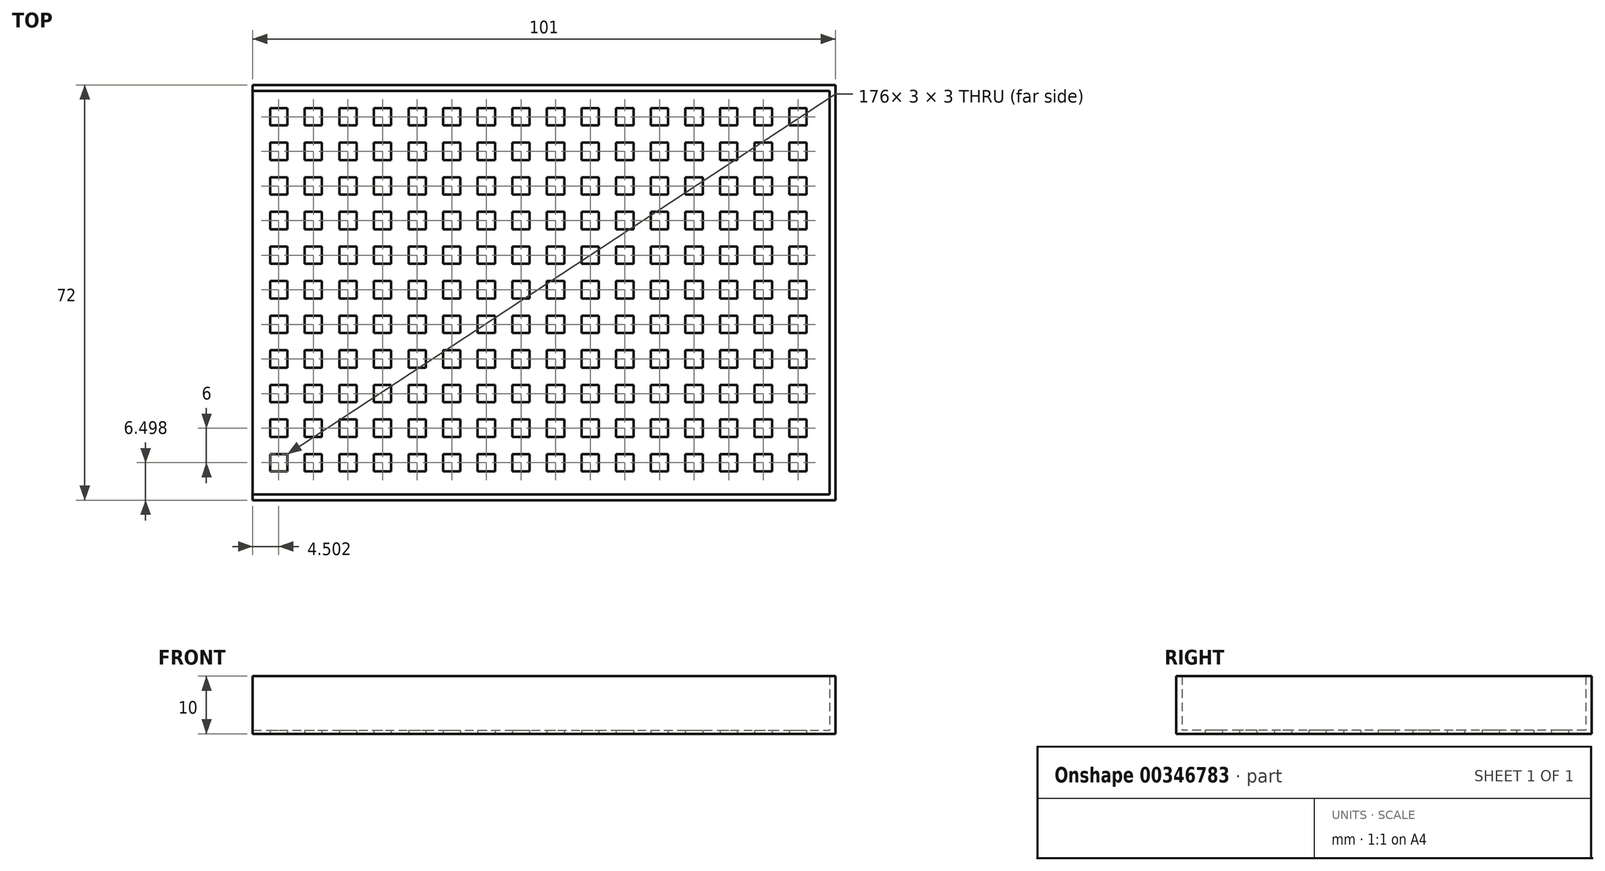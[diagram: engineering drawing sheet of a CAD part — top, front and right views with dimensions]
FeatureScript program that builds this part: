
annotation { "Feature Type Name" : "Feature", "Feature Type Description" : "" }
export const myFeature = defineFeature(function(context is Context, id is Id, definition is map)
    precondition{}
    {
        {
            var Q0;
            Q0=qCreatedBy(makeId("Top.planeOp"),FACE);
            var sketch = newSketch(context, id + "F0", { "sketchPlane" : qUnion([Q0])});
            skLineSegment(sketch, "E0.bottom", {"start": v(-89.09, 32.87) * mm, "end": v(10.91, 32.87) * mm});
            skLineSegment(sketch, "E0.top", {"start": v(-89.09, -37.13) * mm, "end": v(10.91, -37.13) * mm});
            skLineSegment(sketch, "E0.left", {"start": v(-89.09, 32.87) * mm, "end": v(-89.09, -37.13) * mm});
            skLineSegment(sketch, "E0.right", {"start": v(10.91, 32.87) * mm, "end": v(10.91, -37.13) * mm});
            skLineSegment(sketch, "E1.bottom", {"start": v(11.91, -38.13) * mm, "end": v(-89.09, -38.13) * mm});
            skLineSegment(sketch, "E1.top", {"start": v(11.91, 33.87) * mm, "end": v(-89.09, 33.87) * mm});
            skLineSegment(sketch, "E1.left", {"start": v(11.91, -38.13) * mm, "end": v(11.91, 33.87) * mm});
            skLineSegment(sketch, "E1.right", {"start": v(-89.09, -38.13) * mm, "end": v(-89.09, 33.87) * mm});
            skLineSegment(sketch, "E2.bottom", {"start": v(-86.09, 29.87) * mm, "end": v(-83.09, 29.87) * mm});
            skLineSegment(sketch, "E2.top", {"start": v(-86.09, 26.87) * mm, "end": v(-83.09, 26.87) * mm});
            skLineSegment(sketch, "E2.left", {"start": v(-86.09, 29.87) * mm, "end": v(-86.09, 26.87) * mm});
            skLineSegment(sketch, "E2.right", {"start": v(-83.09, 29.87) * mm, "end": v(-83.09, 26.87) * mm});
            skLineSegment(sketch, "E3.0.1.0", {"start": v(-86.09, 23.87) * mm, "end": v(-83.09, 23.87) * mm});
            skLineSegment(sketch, "E3.0.1.1", {"start": v(-86.09, 20.87) * mm, "end": v(-83.09, 20.87) * mm});
            skLineSegment(sketch, "E3.0.1.2", {"start": v(-86.09, 23.87) * mm, "end": v(-86.09, 20.87) * mm});
            skLineSegment(sketch, "E3.0.1.3", {"start": v(-83.09, 23.87) * mm, "end": v(-83.09, 20.87) * mm});
            skLineSegment(sketch, "E3.0.2.0", {"start": v(-86.09, 17.87) * mm, "end": v(-83.09, 17.87) * mm});
            skLineSegment(sketch, "E3.0.2.1", {"start": v(-86.09, 14.87) * mm, "end": v(-83.09, 14.87) * mm});
            skLineSegment(sketch, "E3.0.2.2", {"start": v(-86.09, 17.87) * mm, "end": v(-86.09, 14.87) * mm});
            skLineSegment(sketch, "E3.0.2.3", {"start": v(-83.09, 17.87) * mm, "end": v(-83.09, 14.87) * mm});
            skLineSegment(sketch, "E3.0.3.0", {"start": v(-86.09, 11.87) * mm, "end": v(-83.09, 11.87) * mm});
            skLineSegment(sketch, "E3.0.3.1", {"start": v(-86.09, 8.87) * mm, "end": v(-83.09, 8.87) * mm});
            skLineSegment(sketch, "E3.0.3.2", {"start": v(-86.09, 11.87) * mm, "end": v(-86.09, 8.87) * mm});
            skLineSegment(sketch, "E3.0.3.3", {"start": v(-83.09, 11.87) * mm, "end": v(-83.09, 8.87) * mm});
            skLineSegment(sketch, "E3.0.4.0", {"start": v(-86.09, 5.87) * mm, "end": v(-83.09, 5.87) * mm});
            skLineSegment(sketch, "E3.0.4.1", {"start": v(-86.09, 2.87) * mm, "end": v(-83.09, 2.87) * mm});
            skLineSegment(sketch, "E3.0.4.2", {"start": v(-86.09, 5.87) * mm, "end": v(-86.09, 2.87) * mm});
            skLineSegment(sketch, "E3.0.4.3", {"start": v(-83.09, 5.87) * mm, "end": v(-83.09, 2.87) * mm});
            skLineSegment(sketch, "E3.0.5.0", {"start": v(-86.09, -0.13) * mm, "end": v(-83.09, -0.13) * mm});
            skLineSegment(sketch, "E3.0.5.1", {"start": v(-86.09, -3.13) * mm, "end": v(-83.09, -3.13) * mm});
            skLineSegment(sketch, "E3.0.5.2", {"start": v(-86.09, -0.13) * mm, "end": v(-86.09, -3.13) * mm});
            skLineSegment(sketch, "E3.0.5.3", {"start": v(-83.09, -0.13) * mm, "end": v(-83.09, -3.13) * mm});
            skLineSegment(sketch, "E3.0.6.0", {"start": v(-86.09, -6.13) * mm, "end": v(-83.09, -6.13) * mm});
            skLineSegment(sketch, "E3.0.6.1", {"start": v(-86.09, -9.13) * mm, "end": v(-83.09, -9.13) * mm});
            skLineSegment(sketch, "E3.0.6.2", {"start": v(-86.09, -6.13) * mm, "end": v(-86.09, -9.13) * mm});
            skLineSegment(sketch, "E3.0.6.3", {"start": v(-83.09, -6.13) * mm, "end": v(-83.09, -9.13) * mm});
            skLineSegment(sketch, "E3.0.7.0", {"start": v(-86.09, -12.13) * mm, "end": v(-83.09, -12.13) * mm});
            skLineSegment(sketch, "E3.0.7.1", {"start": v(-86.09, -15.13) * mm, "end": v(-83.09, -15.13) * mm});
            skLineSegment(sketch, "E3.0.7.2", {"start": v(-86.09, -12.13) * mm, "end": v(-86.09, -15.13) * mm});
            skLineSegment(sketch, "E3.0.7.3", {"start": v(-83.09, -12.13) * mm, "end": v(-83.09, -15.13) * mm});
            skLineSegment(sketch, "E3.0.8.0", {"start": v(-86.09, -18.13) * mm, "end": v(-83.09, -18.13) * mm});
            skLineSegment(sketch, "E3.0.8.1", {"start": v(-86.09, -21.13) * mm, "end": v(-83.09, -21.13) * mm});
            skLineSegment(sketch, "E3.0.8.2", {"start": v(-86.09, -18.13) * mm, "end": v(-86.09, -21.13) * mm});
            skLineSegment(sketch, "E3.0.8.3", {"start": v(-83.09, -18.13) * mm, "end": v(-83.09, -21.13) * mm});
            skLineSegment(sketch, "E3.0.9.0", {"start": v(-86.09, -24.13) * mm, "end": v(-83.09, -24.13) * mm});
            skLineSegment(sketch, "E3.0.9.1", {"start": v(-86.09, -27.13) * mm, "end": v(-83.09, -27.13) * mm});
            skLineSegment(sketch, "E3.0.9.2", {"start": v(-86.09, -24.13) * mm, "end": v(-86.09, -27.13) * mm});
            skLineSegment(sketch, "E3.0.9.3", {"start": v(-83.09, -24.13) * mm, "end": v(-83.09, -27.13) * mm});
            skLineSegment(sketch, "E3.1.0.0", {"start": v(-80.09, 29.87) * mm, "end": v(-77.09, 29.87) * mm});
            skLineSegment(sketch, "E3.1.0.1", {"start": v(-80.09, 26.87) * mm, "end": v(-77.09, 26.87) * mm});
            skLineSegment(sketch, "E3.1.0.2", {"start": v(-80.09, 29.87) * mm, "end": v(-80.09, 26.87) * mm});
            skLineSegment(sketch, "E3.1.0.3", {"start": v(-77.09, 29.87) * mm, "end": v(-77.09, 26.87) * mm});
            skLineSegment(sketch, "E3.1.1.0", {"start": v(-80.09, 23.87) * mm, "end": v(-77.09, 23.87) * mm});
            skLineSegment(sketch, "E3.1.1.1", {"start": v(-80.09, 20.87) * mm, "end": v(-77.09, 20.87) * mm});
            skLineSegment(sketch, "E3.1.1.2", {"start": v(-80.09, 23.87) * mm, "end": v(-80.09, 20.87) * mm});
            skLineSegment(sketch, "E3.1.1.3", {"start": v(-77.09, 23.87) * mm, "end": v(-77.09, 20.87) * mm});
            skLineSegment(sketch, "E3.1.2.0", {"start": v(-80.09, 17.87) * mm, "end": v(-77.09, 17.87) * mm});
            skLineSegment(sketch, "E3.1.2.1", {"start": v(-80.09, 14.87) * mm, "end": v(-77.09, 14.87) * mm});
            skLineSegment(sketch, "E3.1.2.2", {"start": v(-80.09, 17.87) * mm, "end": v(-80.09, 14.87) * mm});
            skLineSegment(sketch, "E3.1.2.3", {"start": v(-77.09, 17.87) * mm, "end": v(-77.09, 14.87) * mm});
            skLineSegment(sketch, "E3.1.3.0", {"start": v(-80.09, 11.87) * mm, "end": v(-77.09, 11.87) * mm});
            skLineSegment(sketch, "E3.1.3.1", {"start": v(-80.09, 8.87) * mm, "end": v(-77.09, 8.87) * mm});
            skLineSegment(sketch, "E3.1.3.2", {"start": v(-80.09, 11.87) * mm, "end": v(-80.09, 8.87) * mm});
            skLineSegment(sketch, "E3.1.3.3", {"start": v(-77.09, 11.87) * mm, "end": v(-77.09, 8.87) * mm});
            skLineSegment(sketch, "E3.1.4.0", {"start": v(-80.09, 5.87) * mm, "end": v(-77.09, 5.87) * mm});
            skLineSegment(sketch, "E3.1.4.1", {"start": v(-80.09, 2.87) * mm, "end": v(-77.09, 2.87) * mm});
            skLineSegment(sketch, "E3.1.4.2", {"start": v(-80.09, 5.87) * mm, "end": v(-80.09, 2.87) * mm});
            skLineSegment(sketch, "E3.1.4.3", {"start": v(-77.09, 5.87) * mm, "end": v(-77.09, 2.87) * mm});
            skLineSegment(sketch, "E3.1.5.0", {"start": v(-80.09, -0.13) * mm, "end": v(-77.09, -0.13) * mm});
            skLineSegment(sketch, "E3.1.5.1", {"start": v(-80.09, -3.13) * mm, "end": v(-77.09, -3.13) * mm});
            skLineSegment(sketch, "E3.1.5.2", {"start": v(-80.09, -0.13) * mm, "end": v(-80.09, -3.13) * mm});
            skLineSegment(sketch, "E3.1.5.3", {"start": v(-77.09, -0.13) * mm, "end": v(-77.09, -3.13) * mm});
            skLineSegment(sketch, "E3.1.6.0", {"start": v(-80.09, -6.13) * mm, "end": v(-77.09, -6.13) * mm});
            skLineSegment(sketch, "E3.1.6.1", {"start": v(-80.09, -9.13) * mm, "end": v(-77.09, -9.13) * mm});
            skLineSegment(sketch, "E3.1.6.2", {"start": v(-80.09, -6.13) * mm, "end": v(-80.09, -9.13) * mm});
            skLineSegment(sketch, "E3.1.6.3", {"start": v(-77.09, -6.13) * mm, "end": v(-77.09, -9.13) * mm});
            skLineSegment(sketch, "E3.1.7.0", {"start": v(-80.09, -12.13) * mm, "end": v(-77.09, -12.13) * mm});
            skLineSegment(sketch, "E3.1.7.1", {"start": v(-80.09, -15.13) * mm, "end": v(-77.09, -15.13) * mm});
            skLineSegment(sketch, "E3.1.7.2", {"start": v(-80.09, -12.13) * mm, "end": v(-80.09, -15.13) * mm});
            skLineSegment(sketch, "E3.1.7.3", {"start": v(-77.09, -12.13) * mm, "end": v(-77.09, -15.13) * mm});
            skLineSegment(sketch, "E3.1.8.0", {"start": v(-80.09, -18.13) * mm, "end": v(-77.09, -18.13) * mm});
            skLineSegment(sketch, "E3.1.8.1", {"start": v(-80.09, -21.13) * mm, "end": v(-77.09, -21.13) * mm});
            skLineSegment(sketch, "E3.1.8.2", {"start": v(-80.09, -18.13) * mm, "end": v(-80.09, -21.13) * mm});
            skLineSegment(sketch, "E3.1.8.3", {"start": v(-77.09, -18.13) * mm, "end": v(-77.09, -21.13) * mm});
            skLineSegment(sketch, "E3.1.9.0", {"start": v(-80.09, -24.13) * mm, "end": v(-77.09, -24.13) * mm});
            skLineSegment(sketch, "E3.1.9.1", {"start": v(-80.09, -27.13) * mm, "end": v(-77.09, -27.13) * mm});
            skLineSegment(sketch, "E3.1.9.2", {"start": v(-80.09, -24.13) * mm, "end": v(-80.09, -27.13) * mm});
            skLineSegment(sketch, "E3.1.9.3", {"start": v(-77.09, -24.13) * mm, "end": v(-77.09, -27.13) * mm});
            skLineSegment(sketch, "E3.2.0.0", {"start": v(-74.09, 29.87) * mm, "end": v(-71.09, 29.87) * mm});
            skLineSegment(sketch, "E3.2.0.1", {"start": v(-74.09, 26.87) * mm, "end": v(-71.09, 26.87) * mm});
            skLineSegment(sketch, "E3.2.0.2", {"start": v(-74.09, 29.87) * mm, "end": v(-74.09, 26.87) * mm});
            skLineSegment(sketch, "E3.2.0.3", {"start": v(-71.09, 29.87) * mm, "end": v(-71.09, 26.87) * mm});
            skLineSegment(sketch, "E3.2.1.0", {"start": v(-74.09, 23.87) * mm, "end": v(-71.09, 23.87) * mm});
            skLineSegment(sketch, "E3.2.1.1", {"start": v(-74.09, 20.87) * mm, "end": v(-71.09, 20.87) * mm});
            skLineSegment(sketch, "E3.2.1.2", {"start": v(-74.09, 23.87) * mm, "end": v(-74.09, 20.87) * mm});
            skLineSegment(sketch, "E3.2.1.3", {"start": v(-71.09, 23.87) * mm, "end": v(-71.09, 20.87) * mm});
            skLineSegment(sketch, "E3.2.2.0", {"start": v(-74.09, 17.87) * mm, "end": v(-71.09, 17.87) * mm});
            skLineSegment(sketch, "E3.2.2.1", {"start": v(-74.09, 14.87) * mm, "end": v(-71.09, 14.87) * mm});
            skLineSegment(sketch, "E3.2.2.2", {"start": v(-74.09, 17.87) * mm, "end": v(-74.09, 14.87) * mm});
            skLineSegment(sketch, "E3.2.2.3", {"start": v(-71.09, 17.87) * mm, "end": v(-71.09, 14.87) * mm});
            skLineSegment(sketch, "E3.2.3.0", {"start": v(-74.09, 11.87) * mm, "end": v(-71.09, 11.87) * mm});
            skLineSegment(sketch, "E3.2.3.1", {"start": v(-74.09, 8.87) * mm, "end": v(-71.09, 8.87) * mm});
            skLineSegment(sketch, "E3.2.3.2", {"start": v(-74.09, 11.87) * mm, "end": v(-74.09, 8.87) * mm});
            skLineSegment(sketch, "E3.2.3.3", {"start": v(-71.09, 11.87) * mm, "end": v(-71.09, 8.87) * mm});
            skLineSegment(sketch, "E3.2.4.0", {"start": v(-74.09, 5.87) * mm, "end": v(-71.09, 5.87) * mm});
            skLineSegment(sketch, "E3.2.4.1", {"start": v(-74.09, 2.87) * mm, "end": v(-71.09, 2.87) * mm});
            skLineSegment(sketch, "E3.2.4.2", {"start": v(-74.09, 5.87) * mm, "end": v(-74.09, 2.87) * mm});
            skLineSegment(sketch, "E3.2.4.3", {"start": v(-71.09, 5.87) * mm, "end": v(-71.09, 2.87) * mm});
            skLineSegment(sketch, "E3.2.5.0", {"start": v(-74.09, -0.13) * mm, "end": v(-71.09, -0.13) * mm});
            skLineSegment(sketch, "E3.2.5.1", {"start": v(-74.09, -3.13) * mm, "end": v(-71.09, -3.13) * mm});
            skLineSegment(sketch, "E3.2.5.2", {"start": v(-74.09, -0.13) * mm, "end": v(-74.09, -3.13) * mm});
            skLineSegment(sketch, "E3.2.5.3", {"start": v(-71.09, -0.13) * mm, "end": v(-71.09, -3.13) * mm});
            skLineSegment(sketch, "E3.2.6.0", {"start": v(-74.09, -6.13) * mm, "end": v(-71.09, -6.13) * mm});
            skLineSegment(sketch, "E3.2.6.1", {"start": v(-74.09, -9.13) * mm, "end": v(-71.09, -9.13) * mm});
            skLineSegment(sketch, "E3.2.6.2", {"start": v(-74.09, -6.13) * mm, "end": v(-74.09, -9.13) * mm});
            skLineSegment(sketch, "E3.2.6.3", {"start": v(-71.09, -6.13) * mm, "end": v(-71.09, -9.13) * mm});
            skLineSegment(sketch, "E3.2.7.0", {"start": v(-74.09, -12.13) * mm, "end": v(-71.09, -12.13) * mm});
            skLineSegment(sketch, "E3.2.7.1", {"start": v(-74.09, -15.13) * mm, "end": v(-71.09, -15.13) * mm});
            skLineSegment(sketch, "E3.2.7.2", {"start": v(-74.09, -12.13) * mm, "end": v(-74.09, -15.13) * mm});
            skLineSegment(sketch, "E3.2.7.3", {"start": v(-71.09, -12.13) * mm, "end": v(-71.09, -15.13) * mm});
            skLineSegment(sketch, "E3.2.8.0", {"start": v(-74.09, -18.13) * mm, "end": v(-71.09, -18.13) * mm});
            skLineSegment(sketch, "E3.2.8.1", {"start": v(-74.09, -21.13) * mm, "end": v(-71.09, -21.13) * mm});
            skLineSegment(sketch, "E3.2.8.2", {"start": v(-74.09, -18.13) * mm, "end": v(-74.09, -21.13) * mm});
            skLineSegment(sketch, "E3.2.8.3", {"start": v(-71.09, -18.13) * mm, "end": v(-71.09, -21.13) * mm});
            skLineSegment(sketch, "E3.2.9.0", {"start": v(-74.09, -24.13) * mm, "end": v(-71.09, -24.13) * mm});
            skLineSegment(sketch, "E3.2.9.1", {"start": v(-74.09, -27.13) * mm, "end": v(-71.09, -27.13) * mm});
            skLineSegment(sketch, "E3.2.9.2", {"start": v(-74.09, -24.13) * mm, "end": v(-74.09, -27.13) * mm});
            skLineSegment(sketch, "E3.2.9.3", {"start": v(-71.09, -24.13) * mm, "end": v(-71.09, -27.13) * mm});
            skLineSegment(sketch, "E3.3.0.0", {"start": v(-68.09, 29.87) * mm, "end": v(-65.09, 29.87) * mm});
            skLineSegment(sketch, "E3.3.0.1", {"start": v(-68.09, 26.87) * mm, "end": v(-65.09, 26.87) * mm});
            skLineSegment(sketch, "E3.3.0.2", {"start": v(-68.09, 29.87) * mm, "end": v(-68.09, 26.87) * mm});
            skLineSegment(sketch, "E3.3.0.3", {"start": v(-65.09, 29.87) * mm, "end": v(-65.09, 26.87) * mm});
            skLineSegment(sketch, "E3.3.1.0", {"start": v(-68.09, 23.87) * mm, "end": v(-65.09, 23.87) * mm});
            skLineSegment(sketch, "E3.3.1.1", {"start": v(-68.09, 20.87) * mm, "end": v(-65.09, 20.87) * mm});
            skLineSegment(sketch, "E3.3.1.2", {"start": v(-68.09, 23.87) * mm, "end": v(-68.09, 20.87) * mm});
            skLineSegment(sketch, "E3.3.1.3", {"start": v(-65.09, 23.87) * mm, "end": v(-65.09, 20.87) * mm});
            skLineSegment(sketch, "E3.3.2.0", {"start": v(-68.09, 17.87) * mm, "end": v(-65.09, 17.87) * mm});
            skLineSegment(sketch, "E3.3.2.1", {"start": v(-68.09, 14.87) * mm, "end": v(-65.09, 14.87) * mm});
            skLineSegment(sketch, "E3.3.2.2", {"start": v(-68.09, 17.87) * mm, "end": v(-68.09, 14.87) * mm});
            skLineSegment(sketch, "E3.3.2.3", {"start": v(-65.09, 17.87) * mm, "end": v(-65.09, 14.87) * mm});
            skLineSegment(sketch, "E3.3.3.0", {"start": v(-68.09, 11.87) * mm, "end": v(-65.09, 11.87) * mm});
            skLineSegment(sketch, "E3.3.3.1", {"start": v(-68.09, 8.87) * mm, "end": v(-65.09, 8.87) * mm});
            skLineSegment(sketch, "E3.3.3.2", {"start": v(-68.09, 11.87) * mm, "end": v(-68.09, 8.87) * mm});
            skLineSegment(sketch, "E3.3.3.3", {"start": v(-65.09, 11.87) * mm, "end": v(-65.09, 8.87) * mm});
            skLineSegment(sketch, "E3.3.4.0", {"start": v(-68.09, 5.87) * mm, "end": v(-65.09, 5.87) * mm});
            skLineSegment(sketch, "E3.3.4.1", {"start": v(-68.09, 2.87) * mm, "end": v(-65.09, 2.87) * mm});
            skLineSegment(sketch, "E3.3.4.2", {"start": v(-68.09, 5.87) * mm, "end": v(-68.09, 2.87) * mm});
            skLineSegment(sketch, "E3.3.4.3", {"start": v(-65.09, 5.87) * mm, "end": v(-65.09, 2.87) * mm});
            skLineSegment(sketch, "E3.3.5.0", {"start": v(-68.09, -0.13) * mm, "end": v(-65.09, -0.13) * mm});
            skLineSegment(sketch, "E3.3.5.1", {"start": v(-68.09, -3.13) * mm, "end": v(-65.09, -3.13) * mm});
            skLineSegment(sketch, "E3.3.5.2", {"start": v(-68.09, -0.13) * mm, "end": v(-68.09, -3.13) * mm});
            skLineSegment(sketch, "E3.3.5.3", {"start": v(-65.09, -0.13) * mm, "end": v(-65.09, -3.13) * mm});
            skLineSegment(sketch, "E3.3.6.0", {"start": v(-68.09, -6.13) * mm, "end": v(-65.09, -6.13) * mm});
            skLineSegment(sketch, "E3.3.6.1", {"start": v(-68.09, -9.13) * mm, "end": v(-65.09, -9.13) * mm});
            skLineSegment(sketch, "E3.3.6.2", {"start": v(-68.09, -6.13) * mm, "end": v(-68.09, -9.13) * mm});
            skLineSegment(sketch, "E3.3.6.3", {"start": v(-65.09, -6.13) * mm, "end": v(-65.09, -9.13) * mm});
            skLineSegment(sketch, "E3.3.7.0", {"start": v(-68.09, -12.13) * mm, "end": v(-65.09, -12.13) * mm});
            skLineSegment(sketch, "E3.3.7.1", {"start": v(-68.09, -15.13) * mm, "end": v(-65.09, -15.13) * mm});
            skLineSegment(sketch, "E3.3.7.2", {"start": v(-68.09, -12.13) * mm, "end": v(-68.09, -15.13) * mm});
            skLineSegment(sketch, "E3.3.7.3", {"start": v(-65.09, -12.13) * mm, "end": v(-65.09, -15.13) * mm});
            skLineSegment(sketch, "E3.3.8.0", {"start": v(-68.09, -18.13) * mm, "end": v(-65.09, -18.13) * mm});
            skLineSegment(sketch, "E3.3.8.1", {"start": v(-68.09, -21.13) * mm, "end": v(-65.09, -21.13) * mm});
            skLineSegment(sketch, "E3.3.8.2", {"start": v(-68.09, -18.13) * mm, "end": v(-68.09, -21.13) * mm});
            skLineSegment(sketch, "E3.3.8.3", {"start": v(-65.09, -18.13) * mm, "end": v(-65.09, -21.13) * mm});
            skLineSegment(sketch, "E3.3.9.0", {"start": v(-68.09, -24.13) * mm, "end": v(-65.09, -24.13) * mm});
            skLineSegment(sketch, "E3.3.9.1", {"start": v(-68.09, -27.13) * mm, "end": v(-65.09, -27.13) * mm});
            skLineSegment(sketch, "E3.3.9.2", {"start": v(-68.09, -24.13) * mm, "end": v(-68.09, -27.13) * mm});
            skLineSegment(sketch, "E3.3.9.3", {"start": v(-65.09, -24.13) * mm, "end": v(-65.09, -27.13) * mm});
            skLineSegment(sketch, "E3.4.0.0", {"start": v(-62.09, 29.87) * mm, "end": v(-59.09, 29.87) * mm});
            skLineSegment(sketch, "E3.4.0.1", {"start": v(-62.09, 26.87) * mm, "end": v(-59.09, 26.87) * mm});
            skLineSegment(sketch, "E3.4.0.2", {"start": v(-62.09, 29.87) * mm, "end": v(-62.09, 26.87) * mm});
            skLineSegment(sketch, "E3.4.0.3", {"start": v(-59.09, 29.87) * mm, "end": v(-59.09, 26.87) * mm});
            skLineSegment(sketch, "E3.4.1.0", {"start": v(-62.09, 23.87) * mm, "end": v(-59.09, 23.87) * mm});
            skLineSegment(sketch, "E3.4.1.1", {"start": v(-62.09, 20.87) * mm, "end": v(-59.09, 20.87) * mm});
            skLineSegment(sketch, "E3.4.1.2", {"start": v(-62.09, 23.87) * mm, "end": v(-62.09, 20.87) * mm});
            skLineSegment(sketch, "E3.4.1.3", {"start": v(-59.09, 23.87) * mm, "end": v(-59.09, 20.87) * mm});
            skLineSegment(sketch, "E3.4.2.0", {"start": v(-62.09, 17.87) * mm, "end": v(-59.09, 17.87) * mm});
            skLineSegment(sketch, "E3.4.2.1", {"start": v(-62.09, 14.87) * mm, "end": v(-59.09, 14.87) * mm});
            skLineSegment(sketch, "E3.4.2.2", {"start": v(-62.09, 17.87) * mm, "end": v(-62.09, 14.87) * mm});
            skLineSegment(sketch, "E3.4.2.3", {"start": v(-59.09, 17.87) * mm, "end": v(-59.09, 14.87) * mm});
            skLineSegment(sketch, "E3.4.3.0", {"start": v(-62.09, 11.87) * mm, "end": v(-59.09, 11.87) * mm});
            skLineSegment(sketch, "E3.4.3.1", {"start": v(-62.09, 8.87) * mm, "end": v(-59.09, 8.87) * mm});
            skLineSegment(sketch, "E3.4.3.2", {"start": v(-62.09, 11.87) * mm, "end": v(-62.09, 8.87) * mm});
            skLineSegment(sketch, "E3.4.3.3", {"start": v(-59.09, 11.87) * mm, "end": v(-59.09, 8.87) * mm});
            skLineSegment(sketch, "E3.4.4.0", {"start": v(-62.09, 5.87) * mm, "end": v(-59.09, 5.87) * mm});
            skLineSegment(sketch, "E3.4.4.1", {"start": v(-62.09, 2.87) * mm, "end": v(-59.09, 2.87) * mm});
            skLineSegment(sketch, "E3.4.4.2", {"start": v(-62.09, 5.87) * mm, "end": v(-62.09, 2.87) * mm});
            skLineSegment(sketch, "E3.4.4.3", {"start": v(-59.09, 5.87) * mm, "end": v(-59.09, 2.87) * mm});
            skLineSegment(sketch, "E3.4.5.0", {"start": v(-62.09, -0.13) * mm, "end": v(-59.09, -0.13) * mm});
            skLineSegment(sketch, "E3.4.5.1", {"start": v(-62.09, -3.13) * mm, "end": v(-59.09, -3.13) * mm});
            skLineSegment(sketch, "E3.4.5.2", {"start": v(-62.09, -0.13) * mm, "end": v(-62.09, -3.13) * mm});
            skLineSegment(sketch, "E3.4.5.3", {"start": v(-59.09, -0.13) * mm, "end": v(-59.09, -3.13) * mm});
            skLineSegment(sketch, "E3.4.6.0", {"start": v(-62.09, -6.13) * mm, "end": v(-59.09, -6.13) * mm});
            skLineSegment(sketch, "E3.4.6.1", {"start": v(-62.09, -9.13) * mm, "end": v(-59.09, -9.13) * mm});
            skLineSegment(sketch, "E3.4.6.2", {"start": v(-62.09, -6.13) * mm, "end": v(-62.09, -9.13) * mm});
            skLineSegment(sketch, "E3.4.6.3", {"start": v(-59.09, -6.13) * mm, "end": v(-59.09, -9.13) * mm});
            skLineSegment(sketch, "E3.4.7.0", {"start": v(-62.09, -12.13) * mm, "end": v(-59.09, -12.13) * mm});
            skLineSegment(sketch, "E3.4.7.1", {"start": v(-62.09, -15.13) * mm, "end": v(-59.09, -15.13) * mm});
            skLineSegment(sketch, "E3.4.7.2", {"start": v(-62.09, -12.13) * mm, "end": v(-62.09, -15.13) * mm});
            skLineSegment(sketch, "E3.4.7.3", {"start": v(-59.09, -12.13) * mm, "end": v(-59.09, -15.13) * mm});
            skLineSegment(sketch, "E3.4.8.0", {"start": v(-62.09, -18.13) * mm, "end": v(-59.09, -18.13) * mm});
            skLineSegment(sketch, "E3.4.8.1", {"start": v(-62.09, -21.13) * mm, "end": v(-59.09, -21.13) * mm});
            skLineSegment(sketch, "E3.4.8.2", {"start": v(-62.09, -18.13) * mm, "end": v(-62.09, -21.13) * mm});
            skLineSegment(sketch, "E3.4.8.3", {"start": v(-59.09, -18.13) * mm, "end": v(-59.09, -21.13) * mm});
            skLineSegment(sketch, "E3.4.9.0", {"start": v(-62.09, -24.13) * mm, "end": v(-59.09, -24.13) * mm});
            skLineSegment(sketch, "E3.4.9.1", {"start": v(-62.09, -27.13) * mm, "end": v(-59.09, -27.13) * mm});
            skLineSegment(sketch, "E3.4.9.2", {"start": v(-62.09, -24.13) * mm, "end": v(-62.09, -27.13) * mm});
            skLineSegment(sketch, "E3.4.9.3", {"start": v(-59.09, -24.13) * mm, "end": v(-59.09, -27.13) * mm});
            skLineSegment(sketch, "E3.5.0.0", {"start": v(-56.09, 29.87) * mm, "end": v(-53.09, 29.87) * mm});
            skLineSegment(sketch, "E3.5.0.1", {"start": v(-56.09, 26.87) * mm, "end": v(-53.09, 26.87) * mm});
            skLineSegment(sketch, "E3.5.0.2", {"start": v(-56.09, 29.87) * mm, "end": v(-56.09, 26.87) * mm});
            skLineSegment(sketch, "E3.5.0.3", {"start": v(-53.09, 29.87) * mm, "end": v(-53.09, 26.87) * mm});
            skLineSegment(sketch, "E3.5.1.0", {"start": v(-56.09, 23.87) * mm, "end": v(-53.09, 23.87) * mm});
            skLineSegment(sketch, "E3.5.1.1", {"start": v(-56.09, 20.87) * mm, "end": v(-53.09, 20.87) * mm});
            skLineSegment(sketch, "E3.5.1.2", {"start": v(-56.09, 23.87) * mm, "end": v(-56.09, 20.87) * mm});
            skLineSegment(sketch, "E3.5.1.3", {"start": v(-53.09, 23.87) * mm, "end": v(-53.09, 20.87) * mm});
            skLineSegment(sketch, "E3.5.2.0", {"start": v(-56.09, 17.87) * mm, "end": v(-53.09, 17.87) * mm});
            skLineSegment(sketch, "E3.5.2.1", {"start": v(-56.09, 14.87) * mm, "end": v(-53.09, 14.87) * mm});
            skLineSegment(sketch, "E3.5.2.2", {"start": v(-56.09, 17.87) * mm, "end": v(-56.09, 14.87) * mm});
            skLineSegment(sketch, "E3.5.2.3", {"start": v(-53.09, 17.87) * mm, "end": v(-53.09, 14.87) * mm});
            skLineSegment(sketch, "E3.5.3.0", {"start": v(-56.09, 11.87) * mm, "end": v(-53.09, 11.87) * mm});
            skLineSegment(sketch, "E3.5.3.1", {"start": v(-56.09, 8.87) * mm, "end": v(-53.09, 8.87) * mm});
            skLineSegment(sketch, "E3.5.3.2", {"start": v(-56.09, 11.87) * mm, "end": v(-56.09, 8.87) * mm});
            skLineSegment(sketch, "E3.5.3.3", {"start": v(-53.09, 11.87) * mm, "end": v(-53.09, 8.87) * mm});
            skLineSegment(sketch, "E3.5.4.0", {"start": v(-56.09, 5.87) * mm, "end": v(-53.09, 5.87) * mm});
            skLineSegment(sketch, "E3.5.4.1", {"start": v(-56.09, 2.87) * mm, "end": v(-53.09, 2.87) * mm});
            skLineSegment(sketch, "E3.5.4.2", {"start": v(-56.09, 5.87) * mm, "end": v(-56.09, 2.87) * mm});
            skLineSegment(sketch, "E3.5.4.3", {"start": v(-53.09, 5.87) * mm, "end": v(-53.09, 2.87) * mm});
            skLineSegment(sketch, "E3.5.5.0", {"start": v(-56.09, -0.13) * mm, "end": v(-53.09, -0.13) * mm});
            skLineSegment(sketch, "E3.5.5.1", {"start": v(-56.09, -3.13) * mm, "end": v(-53.09, -3.13) * mm});
            skLineSegment(sketch, "E3.5.5.2", {"start": v(-56.09, -0.13) * mm, "end": v(-56.09, -3.13) * mm});
            skLineSegment(sketch, "E3.5.5.3", {"start": v(-53.09, -0.13) * mm, "end": v(-53.09, -3.13) * mm});
            skLineSegment(sketch, "E3.5.6.0", {"start": v(-56.09, -6.13) * mm, "end": v(-53.09, -6.13) * mm});
            skLineSegment(sketch, "E3.5.6.1", {"start": v(-56.09, -9.13) * mm, "end": v(-53.09, -9.13) * mm});
            skLineSegment(sketch, "E3.5.6.2", {"start": v(-56.09, -6.13) * mm, "end": v(-56.09, -9.13) * mm});
            skLineSegment(sketch, "E3.5.6.3", {"start": v(-53.09, -6.13) * mm, "end": v(-53.09, -9.13) * mm});
            skLineSegment(sketch, "E3.5.7.0", {"start": v(-56.09, -12.13) * mm, "end": v(-53.09, -12.13) * mm});
            skLineSegment(sketch, "E3.5.7.1", {"start": v(-56.09, -15.13) * mm, "end": v(-53.09, -15.13) * mm});
            skLineSegment(sketch, "E3.5.7.2", {"start": v(-56.09, -12.13) * mm, "end": v(-56.09, -15.13) * mm});
            skLineSegment(sketch, "E3.5.7.3", {"start": v(-53.09, -12.13) * mm, "end": v(-53.09, -15.13) * mm});
            skLineSegment(sketch, "E3.5.8.0", {"start": v(-56.09, -18.13) * mm, "end": v(-53.09, -18.13) * mm});
            skLineSegment(sketch, "E3.5.8.1", {"start": v(-56.09, -21.13) * mm, "end": v(-53.09, -21.13) * mm});
            skLineSegment(sketch, "E3.5.8.2", {"start": v(-56.09, -18.13) * mm, "end": v(-56.09, -21.13) * mm});
            skLineSegment(sketch, "E3.5.8.3", {"start": v(-53.09, -18.13) * mm, "end": v(-53.09, -21.13) * mm});
            skLineSegment(sketch, "E3.5.9.0", {"start": v(-56.09, -24.13) * mm, "end": v(-53.09, -24.13) * mm});
            skLineSegment(sketch, "E3.5.9.1", {"start": v(-56.09, -27.13) * mm, "end": v(-53.09, -27.13) * mm});
            skLineSegment(sketch, "E3.5.9.2", {"start": v(-56.09, -24.13) * mm, "end": v(-56.09, -27.13) * mm});
            skLineSegment(sketch, "E3.5.9.3", {"start": v(-53.09, -24.13) * mm, "end": v(-53.09, -27.13) * mm});
            skLineSegment(sketch, "E3.6.0.0", {"start": v(-50.09, 29.87) * mm, "end": v(-47.09, 29.87) * mm});
            skLineSegment(sketch, "E3.6.0.1", {"start": v(-50.09, 26.87) * mm, "end": v(-47.09, 26.87) * mm});
            skLineSegment(sketch, "E3.6.0.2", {"start": v(-50.09, 29.87) * mm, "end": v(-50.09, 26.87) * mm});
            skLineSegment(sketch, "E3.6.0.3", {"start": v(-47.09, 29.87) * mm, "end": v(-47.09, 26.87) * mm});
            skLineSegment(sketch, "E3.6.1.0", {"start": v(-50.09, 23.87) * mm, "end": v(-47.09, 23.87) * mm});
            skLineSegment(sketch, "E3.6.1.1", {"start": v(-50.09, 20.87) * mm, "end": v(-47.09, 20.87) * mm});
            skLineSegment(sketch, "E3.6.1.2", {"start": v(-50.09, 23.87) * mm, "end": v(-50.09, 20.87) * mm});
            skLineSegment(sketch, "E3.6.1.3", {"start": v(-47.09, 23.87) * mm, "end": v(-47.09, 20.87) * mm});
            skLineSegment(sketch, "E3.6.2.0", {"start": v(-50.09, 17.87) * mm, "end": v(-47.09, 17.87) * mm});
            skLineSegment(sketch, "E3.6.2.1", {"start": v(-50.09, 14.87) * mm, "end": v(-47.09, 14.87) * mm});
            skLineSegment(sketch, "E3.6.2.2", {"start": v(-50.09, 17.87) * mm, "end": v(-50.09, 14.87) * mm});
            skLineSegment(sketch, "E3.6.2.3", {"start": v(-47.09, 17.87) * mm, "end": v(-47.09, 14.87) * mm});
            skLineSegment(sketch, "E3.6.3.0", {"start": v(-50.09, 11.87) * mm, "end": v(-47.09, 11.87) * mm});
            skLineSegment(sketch, "E3.6.3.1", {"start": v(-50.09, 8.87) * mm, "end": v(-47.09, 8.87) * mm});
            skLineSegment(sketch, "E3.6.3.2", {"start": v(-50.09, 11.87) * mm, "end": v(-50.09, 8.87) * mm});
            skLineSegment(sketch, "E3.6.3.3", {"start": v(-47.09, 11.87) * mm, "end": v(-47.09, 8.87) * mm});
            skLineSegment(sketch, "E3.6.4.0", {"start": v(-50.09, 5.87) * mm, "end": v(-47.09, 5.87) * mm});
            skLineSegment(sketch, "E3.6.4.1", {"start": v(-50.09, 2.87) * mm, "end": v(-47.09, 2.87) * mm});
            skLineSegment(sketch, "E3.6.4.2", {"start": v(-50.09, 5.87) * mm, "end": v(-50.09, 2.87) * mm});
            skLineSegment(sketch, "E3.6.4.3", {"start": v(-47.09, 5.87) * mm, "end": v(-47.09, 2.87) * mm});
            skLineSegment(sketch, "E3.6.5.0", {"start": v(-50.09, -0.13) * mm, "end": v(-47.09, -0.13) * mm});
            skLineSegment(sketch, "E3.6.5.1", {"start": v(-50.09, -3.13) * mm, "end": v(-47.09, -3.13) * mm});
            skLineSegment(sketch, "E3.6.5.2", {"start": v(-50.09, -0.13) * mm, "end": v(-50.09, -3.13) * mm});
            skLineSegment(sketch, "E3.6.5.3", {"start": v(-47.09, -0.13) * mm, "end": v(-47.09, -3.13) * mm});
            skLineSegment(sketch, "E3.6.6.0", {"start": v(-50.09, -6.13) * mm, "end": v(-47.09, -6.13) * mm});
            skLineSegment(sketch, "E3.6.6.1", {"start": v(-50.09, -9.13) * mm, "end": v(-47.09, -9.13) * mm});
            skLineSegment(sketch, "E3.6.6.2", {"start": v(-50.09, -6.13) * mm, "end": v(-50.09, -9.13) * mm});
            skLineSegment(sketch, "E3.6.6.3", {"start": v(-47.09, -6.13) * mm, "end": v(-47.09, -9.13) * mm});
            skLineSegment(sketch, "E3.6.7.0", {"start": v(-50.09, -12.13) * mm, "end": v(-47.09, -12.13) * mm});
            skLineSegment(sketch, "E3.6.7.1", {"start": v(-50.09, -15.13) * mm, "end": v(-47.09, -15.13) * mm});
            skLineSegment(sketch, "E3.6.7.2", {"start": v(-50.09, -12.13) * mm, "end": v(-50.09, -15.13) * mm});
            skLineSegment(sketch, "E3.6.7.3", {"start": v(-47.09, -12.13) * mm, "end": v(-47.09, -15.13) * mm});
            skLineSegment(sketch, "E3.6.8.0", {"start": v(-50.09, -18.13) * mm, "end": v(-47.09, -18.13) * mm});
            skLineSegment(sketch, "E3.6.8.1", {"start": v(-50.09, -21.13) * mm, "end": v(-47.09, -21.13) * mm});
            skLineSegment(sketch, "E3.6.8.2", {"start": v(-50.09, -18.13) * mm, "end": v(-50.09, -21.13) * mm});
            skLineSegment(sketch, "E3.6.8.3", {"start": v(-47.09, -18.13) * mm, "end": v(-47.09, -21.13) * mm});
            skLineSegment(sketch, "E3.6.9.0", {"start": v(-50.09, -24.13) * mm, "end": v(-47.09, -24.13) * mm});
            skLineSegment(sketch, "E3.6.9.1", {"start": v(-50.09, -27.13) * mm, "end": v(-47.09, -27.13) * mm});
            skLineSegment(sketch, "E3.6.9.2", {"start": v(-50.09, -24.13) * mm, "end": v(-50.09, -27.13) * mm});
            skLineSegment(sketch, "E3.6.9.3", {"start": v(-47.09, -24.13) * mm, "end": v(-47.09, -27.13) * mm});
            skLineSegment(sketch, "E3.7.0.0", {"start": v(-44.09, 29.87) * mm, "end": v(-41.09, 29.87) * mm});
            skLineSegment(sketch, "E3.7.0.1", {"start": v(-44.09, 26.87) * mm, "end": v(-41.09, 26.87) * mm});
            skLineSegment(sketch, "E3.7.0.2", {"start": v(-44.09, 29.87) * mm, "end": v(-44.09, 26.87) * mm});
            skLineSegment(sketch, "E3.7.0.3", {"start": v(-41.09, 29.87) * mm, "end": v(-41.09, 26.87) * mm});
            skLineSegment(sketch, "E3.7.1.0", {"start": v(-44.09, 23.87) * mm, "end": v(-41.09, 23.87) * mm});
            skLineSegment(sketch, "E3.7.1.1", {"start": v(-44.09, 20.87) * mm, "end": v(-41.09, 20.87) * mm});
            skLineSegment(sketch, "E3.7.1.2", {"start": v(-44.09, 23.87) * mm, "end": v(-44.09, 20.87) * mm});
            skLineSegment(sketch, "E3.7.1.3", {"start": v(-41.09, 23.87) * mm, "end": v(-41.09, 20.87) * mm});
            skLineSegment(sketch, "E3.7.2.0", {"start": v(-44.09, 17.87) * mm, "end": v(-41.09, 17.87) * mm});
            skLineSegment(sketch, "E3.7.2.1", {"start": v(-44.09, 14.87) * mm, "end": v(-41.09, 14.87) * mm});
            skLineSegment(sketch, "E3.7.2.2", {"start": v(-44.09, 17.87) * mm, "end": v(-44.09, 14.87) * mm});
            skLineSegment(sketch, "E3.7.2.3", {"start": v(-41.09, 17.87) * mm, "end": v(-41.09, 14.87) * mm});
            skLineSegment(sketch, "E3.7.3.0", {"start": v(-44.09, 11.87) * mm, "end": v(-41.09, 11.87) * mm});
            skLineSegment(sketch, "E3.7.3.1", {"start": v(-44.09, 8.87) * mm, "end": v(-41.09, 8.87) * mm});
            skLineSegment(sketch, "E3.7.3.2", {"start": v(-44.09, 11.87) * mm, "end": v(-44.09, 8.87) * mm});
            skLineSegment(sketch, "E3.7.3.3", {"start": v(-41.09, 11.87) * mm, "end": v(-41.09, 8.87) * mm});
            skLineSegment(sketch, "E3.7.4.0", {"start": v(-44.09, 5.87) * mm, "end": v(-41.09, 5.87) * mm});
            skLineSegment(sketch, "E3.7.4.1", {"start": v(-44.09, 2.87) * mm, "end": v(-41.09, 2.87) * mm});
            skLineSegment(sketch, "E3.7.4.2", {"start": v(-44.09, 5.87) * mm, "end": v(-44.09, 2.87) * mm});
            skLineSegment(sketch, "E3.7.4.3", {"start": v(-41.09, 5.87) * mm, "end": v(-41.09, 2.87) * mm});
            skLineSegment(sketch, "E3.7.5.0", {"start": v(-44.09, -0.13) * mm, "end": v(-41.09, -0.13) * mm});
            skLineSegment(sketch, "E3.7.5.1", {"start": v(-44.09, -3.13) * mm, "end": v(-41.09, -3.13) * mm});
            skLineSegment(sketch, "E3.7.5.2", {"start": v(-44.09, -0.13) * mm, "end": v(-44.09, -3.13) * mm});
            skLineSegment(sketch, "E3.7.5.3", {"start": v(-41.09, -0.13) * mm, "end": v(-41.09, -3.13) * mm});
            skLineSegment(sketch, "E3.7.6.0", {"start": v(-44.09, -6.13) * mm, "end": v(-41.09, -6.13) * mm});
            skLineSegment(sketch, "E3.7.6.1", {"start": v(-44.09, -9.13) * mm, "end": v(-41.09, -9.13) * mm});
            skLineSegment(sketch, "E3.7.6.2", {"start": v(-44.09, -6.13) * mm, "end": v(-44.09, -9.13) * mm});
            skLineSegment(sketch, "E3.7.6.3", {"start": v(-41.09, -6.13) * mm, "end": v(-41.09, -9.13) * mm});
            skLineSegment(sketch, "E3.7.7.0", {"start": v(-44.09, -12.13) * mm, "end": v(-41.09, -12.13) * mm});
            skLineSegment(sketch, "E3.7.7.1", {"start": v(-44.09, -15.13) * mm, "end": v(-41.09, -15.13) * mm});
            skLineSegment(sketch, "E3.7.7.2", {"start": v(-44.09, -12.13) * mm, "end": v(-44.09, -15.13) * mm});
            skLineSegment(sketch, "E3.7.7.3", {"start": v(-41.09, -12.13) * mm, "end": v(-41.09, -15.13) * mm});
            skLineSegment(sketch, "E3.7.8.0", {"start": v(-44.09, -18.13) * mm, "end": v(-41.09, -18.13) * mm});
            skLineSegment(sketch, "E3.7.8.1", {"start": v(-44.09, -21.13) * mm, "end": v(-41.09, -21.13) * mm});
            skLineSegment(sketch, "E3.7.8.2", {"start": v(-44.09, -18.13) * mm, "end": v(-44.09, -21.13) * mm});
            skLineSegment(sketch, "E3.7.8.3", {"start": v(-41.09, -18.13) * mm, "end": v(-41.09, -21.13) * mm});
            skLineSegment(sketch, "E3.7.9.0", {"start": v(-44.09, -24.13) * mm, "end": v(-41.09, -24.13) * mm});
            skLineSegment(sketch, "E3.7.9.1", {"start": v(-44.09, -27.13) * mm, "end": v(-41.09, -27.13) * mm});
            skLineSegment(sketch, "E3.7.9.2", {"start": v(-44.09, -24.13) * mm, "end": v(-44.09, -27.13) * mm});
            skLineSegment(sketch, "E3.7.9.3", {"start": v(-41.09, -24.13) * mm, "end": v(-41.09, -27.13) * mm});
            skLineSegment(sketch, "E3.8.0.0", {"start": v(-38.09, 29.87) * mm, "end": v(-35.09, 29.87) * mm});
            skLineSegment(sketch, "E3.8.0.1", {"start": v(-38.09, 26.87) * mm, "end": v(-35.09, 26.87) * mm});
            skLineSegment(sketch, "E3.8.0.2", {"start": v(-38.09, 29.87) * mm, "end": v(-38.09, 26.87) * mm});
            skLineSegment(sketch, "E3.8.0.3", {"start": v(-35.09, 29.87) * mm, "end": v(-35.09, 26.87) * mm});
            skLineSegment(sketch, "E3.8.1.0", {"start": v(-38.09, 23.87) * mm, "end": v(-35.09, 23.87) * mm});
            skLineSegment(sketch, "E3.8.1.1", {"start": v(-38.09, 20.87) * mm, "end": v(-35.09, 20.87) * mm});
            skLineSegment(sketch, "E3.8.1.2", {"start": v(-38.09, 23.87) * mm, "end": v(-38.09, 20.87) * mm});
            skLineSegment(sketch, "E3.8.1.3", {"start": v(-35.09, 23.87) * mm, "end": v(-35.09, 20.87) * mm});
            skLineSegment(sketch, "E3.8.2.0", {"start": v(-38.09, 17.87) * mm, "end": v(-35.09, 17.87) * mm});
            skLineSegment(sketch, "E3.8.2.1", {"start": v(-38.09, 14.87) * mm, "end": v(-35.09, 14.87) * mm});
            skLineSegment(sketch, "E3.8.2.2", {"start": v(-38.09, 17.87) * mm, "end": v(-38.09, 14.87) * mm});
            skLineSegment(sketch, "E3.8.2.3", {"start": v(-35.09, 17.87) * mm, "end": v(-35.09, 14.87) * mm});
            skLineSegment(sketch, "E3.8.3.0", {"start": v(-38.09, 11.87) * mm, "end": v(-35.09, 11.87) * mm});
            skLineSegment(sketch, "E3.8.3.1", {"start": v(-38.09, 8.87) * mm, "end": v(-35.09, 8.87) * mm});
            skLineSegment(sketch, "E3.8.3.2", {"start": v(-38.09, 11.87) * mm, "end": v(-38.09, 8.87) * mm});
            skLineSegment(sketch, "E3.8.3.3", {"start": v(-35.09, 11.87) * mm, "end": v(-35.09, 8.87) * mm});
            skLineSegment(sketch, "E3.8.4.0", {"start": v(-38.09, 5.87) * mm, "end": v(-35.09, 5.87) * mm});
            skLineSegment(sketch, "E3.8.4.1", {"start": v(-38.09, 2.87) * mm, "end": v(-35.09, 2.87) * mm});
            skLineSegment(sketch, "E3.8.4.2", {"start": v(-38.09, 5.87) * mm, "end": v(-38.09, 2.87) * mm});
            skLineSegment(sketch, "E3.8.4.3", {"start": v(-35.09, 5.87) * mm, "end": v(-35.09, 2.87) * mm});
            skLineSegment(sketch, "E3.8.5.0", {"start": v(-38.09, -0.13) * mm, "end": v(-35.09, -0.13) * mm});
            skLineSegment(sketch, "E3.8.5.1", {"start": v(-38.09, -3.13) * mm, "end": v(-35.09, -3.13) * mm});
            skLineSegment(sketch, "E3.8.5.2", {"start": v(-38.09, -0.13) * mm, "end": v(-38.09, -3.13) * mm});
            skLineSegment(sketch, "E3.8.5.3", {"start": v(-35.09, -0.13) * mm, "end": v(-35.09, -3.13) * mm});
            skLineSegment(sketch, "E3.8.6.0", {"start": v(-38.09, -6.13) * mm, "end": v(-35.09, -6.13) * mm});
            skLineSegment(sketch, "E3.8.6.1", {"start": v(-38.09, -9.13) * mm, "end": v(-35.09, -9.13) * mm});
            skLineSegment(sketch, "E3.8.6.2", {"start": v(-38.09, -6.13) * mm, "end": v(-38.09, -9.13) * mm});
            skLineSegment(sketch, "E3.8.6.3", {"start": v(-35.09, -6.13) * mm, "end": v(-35.09, -9.13) * mm});
            skLineSegment(sketch, "E3.8.7.0", {"start": v(-38.09, -12.13) * mm, "end": v(-35.09, -12.13) * mm});
            skLineSegment(sketch, "E3.8.7.1", {"start": v(-38.09, -15.13) * mm, "end": v(-35.09, -15.13) * mm});
            skLineSegment(sketch, "E3.8.7.2", {"start": v(-38.09, -12.13) * mm, "end": v(-38.09, -15.13) * mm});
            skLineSegment(sketch, "E3.8.7.3", {"start": v(-35.09, -12.13) * mm, "end": v(-35.09, -15.13) * mm});
            skLineSegment(sketch, "E3.8.8.0", {"start": v(-38.09, -18.13) * mm, "end": v(-35.09, -18.13) * mm});
            skLineSegment(sketch, "E3.8.8.1", {"start": v(-38.09, -21.13) * mm, "end": v(-35.09, -21.13) * mm});
            skLineSegment(sketch, "E3.8.8.2", {"start": v(-38.09, -18.13) * mm, "end": v(-38.09, -21.13) * mm});
            skLineSegment(sketch, "E3.8.8.3", {"start": v(-35.09, -18.13) * mm, "end": v(-35.09, -21.13) * mm});
            skLineSegment(sketch, "E3.8.9.0", {"start": v(-38.09, -24.13) * mm, "end": v(-35.09, -24.13) * mm});
            skLineSegment(sketch, "E3.8.9.1", {"start": v(-38.09, -27.13) * mm, "end": v(-35.09, -27.13) * mm});
            skLineSegment(sketch, "E3.8.9.2", {"start": v(-38.09, -24.13) * mm, "end": v(-38.09, -27.13) * mm});
            skLineSegment(sketch, "E3.8.9.3", {"start": v(-35.09, -24.13) * mm, "end": v(-35.09, -27.13) * mm});
            skLineSegment(sketch, "E3.9.0.0", {"start": v(-32.09, 29.87) * mm, "end": v(-29.09, 29.87) * mm});
            skLineSegment(sketch, "E3.9.0.1", {"start": v(-32.09, 26.87) * mm, "end": v(-29.09, 26.87) * mm});
            skLineSegment(sketch, "E3.9.0.2", {"start": v(-32.09, 29.87) * mm, "end": v(-32.09, 26.87) * mm});
            skLineSegment(sketch, "E3.9.0.3", {"start": v(-29.09, 29.87) * mm, "end": v(-29.09, 26.87) * mm});
            skLineSegment(sketch, "E3.9.1.0", {"start": v(-32.09, 23.87) * mm, "end": v(-29.09, 23.87) * mm});
            skLineSegment(sketch, "E3.9.1.1", {"start": v(-32.09, 20.87) * mm, "end": v(-29.09, 20.87) * mm});
            skLineSegment(sketch, "E3.9.1.2", {"start": v(-32.09, 23.87) * mm, "end": v(-32.09, 20.87) * mm});
            skLineSegment(sketch, "E3.9.1.3", {"start": v(-29.09, 23.87) * mm, "end": v(-29.09, 20.87) * mm});
            skLineSegment(sketch, "E3.9.2.0", {"start": v(-32.09, 17.87) * mm, "end": v(-29.09, 17.87) * mm});
            skLineSegment(sketch, "E3.9.2.1", {"start": v(-32.09, 14.87) * mm, "end": v(-29.09, 14.87) * mm});
            skLineSegment(sketch, "E3.9.2.2", {"start": v(-32.09, 17.87) * mm, "end": v(-32.09, 14.87) * mm});
            skLineSegment(sketch, "E3.9.2.3", {"start": v(-29.09, 17.87) * mm, "end": v(-29.09, 14.87) * mm});
            skLineSegment(sketch, "E3.9.3.0", {"start": v(-32.09, 11.87) * mm, "end": v(-29.09, 11.87) * mm});
            skLineSegment(sketch, "E3.9.3.1", {"start": v(-32.09, 8.87) * mm, "end": v(-29.09, 8.87) * mm});
            skLineSegment(sketch, "E3.9.3.2", {"start": v(-32.09, 11.87) * mm, "end": v(-32.09, 8.87) * mm});
            skLineSegment(sketch, "E3.9.3.3", {"start": v(-29.09, 11.87) * mm, "end": v(-29.09, 8.87) * mm});
            skLineSegment(sketch, "E3.9.4.0", {"start": v(-32.09, 5.87) * mm, "end": v(-29.09, 5.87) * mm});
            skLineSegment(sketch, "E3.9.4.1", {"start": v(-32.09, 2.87) * mm, "end": v(-29.09, 2.87) * mm});
            skLineSegment(sketch, "E3.9.4.2", {"start": v(-32.09, 5.87) * mm, "end": v(-32.09, 2.87) * mm});
            skLineSegment(sketch, "E3.9.4.3", {"start": v(-29.09, 5.87) * mm, "end": v(-29.09, 2.87) * mm});
            skLineSegment(sketch, "E3.9.5.0", {"start": v(-32.09, -0.13) * mm, "end": v(-29.09, -0.13) * mm});
            skLineSegment(sketch, "E3.9.5.1", {"start": v(-32.09, -3.13) * mm, "end": v(-29.09, -3.13) * mm});
            skLineSegment(sketch, "E3.9.5.2", {"start": v(-32.09, -0.13) * mm, "end": v(-32.09, -3.13) * mm});
            skLineSegment(sketch, "E3.9.5.3", {"start": v(-29.09, -0.13) * mm, "end": v(-29.09, -3.13) * mm});
            skLineSegment(sketch, "E3.9.6.0", {"start": v(-32.09, -6.13) * mm, "end": v(-29.09, -6.13) * mm});
            skLineSegment(sketch, "E3.9.6.1", {"start": v(-32.09, -9.13) * mm, "end": v(-29.09, -9.13) * mm});
            skLineSegment(sketch, "E3.9.6.2", {"start": v(-32.09, -6.13) * mm, "end": v(-32.09, -9.13) * mm});
            skLineSegment(sketch, "E3.9.6.3", {"start": v(-29.09, -6.13) * mm, "end": v(-29.09, -9.13) * mm});
            skLineSegment(sketch, "E3.9.7.0", {"start": v(-32.09, -12.13) * mm, "end": v(-29.09, -12.13) * mm});
            skLineSegment(sketch, "E3.9.7.1", {"start": v(-32.09, -15.13) * mm, "end": v(-29.09, -15.13) * mm});
            skLineSegment(sketch, "E3.9.7.2", {"start": v(-32.09, -12.13) * mm, "end": v(-32.09, -15.13) * mm});
            skLineSegment(sketch, "E3.9.7.3", {"start": v(-29.09, -12.13) * mm, "end": v(-29.09, -15.13) * mm});
            skLineSegment(sketch, "E3.9.8.0", {"start": v(-32.09, -18.13) * mm, "end": v(-29.09, -18.13) * mm});
            skLineSegment(sketch, "E3.9.8.1", {"start": v(-32.09, -21.13) * mm, "end": v(-29.09, -21.13) * mm});
            skLineSegment(sketch, "E3.9.8.2", {"start": v(-32.09, -18.13) * mm, "end": v(-32.09, -21.13) * mm});
            skLineSegment(sketch, "E3.9.8.3", {"start": v(-29.09, -18.13) * mm, "end": v(-29.09, -21.13) * mm});
            skLineSegment(sketch, "E3.9.9.0", {"start": v(-32.09, -24.13) * mm, "end": v(-29.09, -24.13) * mm});
            skLineSegment(sketch, "E3.9.9.1", {"start": v(-32.09, -27.13) * mm, "end": v(-29.09, -27.13) * mm});
            skLineSegment(sketch, "E3.9.9.2", {"start": v(-32.09, -24.13) * mm, "end": v(-32.09, -27.13) * mm});
            skLineSegment(sketch, "E3.9.9.3", {"start": v(-29.09, -24.13) * mm, "end": v(-29.09, -27.13) * mm});
            skLineSegment(sketch, "E3.10.0.0", {"start": v(-26.09, 29.87) * mm, "end": v(-23.09, 29.87) * mm});
            skLineSegment(sketch, "E3.10.0.1", {"start": v(-26.09, 26.87) * mm, "end": v(-23.09, 26.87) * mm});
            skLineSegment(sketch, "E3.10.0.2", {"start": v(-26.09, 29.87) * mm, "end": v(-26.09, 26.87) * mm});
            skLineSegment(sketch, "E3.10.0.3", {"start": v(-23.09, 29.87) * mm, "end": v(-23.09, 26.87) * mm});
            skLineSegment(sketch, "E3.10.1.0", {"start": v(-26.09, 23.87) * mm, "end": v(-23.09, 23.87) * mm});
            skLineSegment(sketch, "E3.10.1.1", {"start": v(-26.09, 20.87) * mm, "end": v(-23.09, 20.87) * mm});
            skLineSegment(sketch, "E3.10.1.2", {"start": v(-26.09, 23.87) * mm, "end": v(-26.09, 20.87) * mm});
            skLineSegment(sketch, "E3.10.1.3", {"start": v(-23.09, 23.87) * mm, "end": v(-23.09, 20.87) * mm});
            skLineSegment(sketch, "E3.10.2.0", {"start": v(-26.09, 17.87) * mm, "end": v(-23.09, 17.87) * mm});
            skLineSegment(sketch, "E3.10.2.1", {"start": v(-26.09, 14.87) * mm, "end": v(-23.09, 14.87) * mm});
            skLineSegment(sketch, "E3.10.2.2", {"start": v(-26.09, 17.87) * mm, "end": v(-26.09, 14.87) * mm});
            skLineSegment(sketch, "E3.10.2.3", {"start": v(-23.09, 17.87) * mm, "end": v(-23.09, 14.87) * mm});
            skLineSegment(sketch, "E3.10.3.0", {"start": v(-26.09, 11.87) * mm, "end": v(-23.09, 11.87) * mm});
            skLineSegment(sketch, "E3.10.3.1", {"start": v(-26.09, 8.87) * mm, "end": v(-23.09, 8.87) * mm});
            skLineSegment(sketch, "E3.10.3.2", {"start": v(-26.09, 11.87) * mm, "end": v(-26.09, 8.87) * mm});
            skLineSegment(sketch, "E3.10.3.3", {"start": v(-23.09, 11.87) * mm, "end": v(-23.09, 8.87) * mm});
            skLineSegment(sketch, "E3.10.4.0", {"start": v(-26.09, 5.87) * mm, "end": v(-23.09, 5.87) * mm});
            skLineSegment(sketch, "E3.10.4.1", {"start": v(-26.09, 2.87) * mm, "end": v(-23.09, 2.87) * mm});
            skLineSegment(sketch, "E3.10.4.2", {"start": v(-26.09, 5.87) * mm, "end": v(-26.09, 2.87) * mm});
            skLineSegment(sketch, "E3.10.4.3", {"start": v(-23.09, 5.87) * mm, "end": v(-23.09, 2.87) * mm});
            skLineSegment(sketch, "E3.10.5.0", {"start": v(-26.09, -0.13) * mm, "end": v(-23.09, -0.13) * mm});
            skLineSegment(sketch, "E3.10.5.1", {"start": v(-26.09, -3.13) * mm, "end": v(-23.09, -3.13) * mm});
            skLineSegment(sketch, "E3.10.5.2", {"start": v(-26.09, -0.13) * mm, "end": v(-26.09, -3.13) * mm});
            skLineSegment(sketch, "E3.10.5.3", {"start": v(-23.09, -0.13) * mm, "end": v(-23.09, -3.13) * mm});
            skLineSegment(sketch, "E3.10.6.0", {"start": v(-26.09, -6.13) * mm, "end": v(-23.09, -6.13) * mm});
            skLineSegment(sketch, "E3.10.6.1", {"start": v(-26.09, -9.13) * mm, "end": v(-23.09, -9.13) * mm});
            skLineSegment(sketch, "E3.10.6.2", {"start": v(-26.09, -6.13) * mm, "end": v(-26.09, -9.13) * mm});
            skLineSegment(sketch, "E3.10.6.3", {"start": v(-23.09, -6.13) * mm, "end": v(-23.09, -9.13) * mm});
            skLineSegment(sketch, "E3.10.7.0", {"start": v(-26.09, -12.13) * mm, "end": v(-23.09, -12.13) * mm});
            skLineSegment(sketch, "E3.10.7.1", {"start": v(-26.09, -15.13) * mm, "end": v(-23.09, -15.13) * mm});
            skLineSegment(sketch, "E3.10.7.2", {"start": v(-26.09, -12.13) * mm, "end": v(-26.09, -15.13) * mm});
            skLineSegment(sketch, "E3.10.7.3", {"start": v(-23.09, -12.13) * mm, "end": v(-23.09, -15.13) * mm});
            skLineSegment(sketch, "E3.10.8.0", {"start": v(-26.09, -18.13) * mm, "end": v(-23.09, -18.13) * mm});
            skLineSegment(sketch, "E3.10.8.1", {"start": v(-26.09, -21.13) * mm, "end": v(-23.09, -21.13) * mm});
            skLineSegment(sketch, "E3.10.8.2", {"start": v(-26.09, -18.13) * mm, "end": v(-26.09, -21.13) * mm});
            skLineSegment(sketch, "E3.10.8.3", {"start": v(-23.09, -18.13) * mm, "end": v(-23.09, -21.13) * mm});
            skLineSegment(sketch, "E3.10.9.0", {"start": v(-26.09, -24.13) * mm, "end": v(-23.09, -24.13) * mm});
            skLineSegment(sketch, "E3.10.9.1", {"start": v(-26.09, -27.13) * mm, "end": v(-23.09, -27.13) * mm});
            skLineSegment(sketch, "E3.10.9.2", {"start": v(-26.09, -24.13) * mm, "end": v(-26.09, -27.13) * mm});
            skLineSegment(sketch, "E3.10.9.3", {"start": v(-23.09, -24.13) * mm, "end": v(-23.09, -27.13) * mm});
            skLineSegment(sketch, "E3.11.0.0", {"start": v(-20.09, 29.87) * mm, "end": v(-17.09, 29.87) * mm});
            skLineSegment(sketch, "E3.11.0.1", {"start": v(-20.09, 26.87) * mm, "end": v(-17.09, 26.87) * mm});
            skLineSegment(sketch, "E3.11.0.2", {"start": v(-20.09, 29.87) * mm, "end": v(-20.09, 26.87) * mm});
            skLineSegment(sketch, "E3.11.0.3", {"start": v(-17.09, 29.87) * mm, "end": v(-17.09, 26.87) * mm});
            skLineSegment(sketch, "E3.11.1.0", {"start": v(-20.09, 23.87) * mm, "end": v(-17.09, 23.87) * mm});
            skLineSegment(sketch, "E3.11.1.1", {"start": v(-20.09, 20.87) * mm, "end": v(-17.09, 20.87) * mm});
            skLineSegment(sketch, "E3.11.1.2", {"start": v(-20.09, 23.87) * mm, "end": v(-20.09, 20.87) * mm});
            skLineSegment(sketch, "E3.11.1.3", {"start": v(-17.09, 23.87) * mm, "end": v(-17.09, 20.87) * mm});
            skLineSegment(sketch, "E3.11.2.0", {"start": v(-20.09, 17.87) * mm, "end": v(-17.09, 17.87) * mm});
            skLineSegment(sketch, "E3.11.2.1", {"start": v(-20.09, 14.87) * mm, "end": v(-17.09, 14.87) * mm});
            skLineSegment(sketch, "E3.11.2.2", {"start": v(-20.09, 17.87) * mm, "end": v(-20.09, 14.87) * mm});
            skLineSegment(sketch, "E3.11.2.3", {"start": v(-17.09, 17.87) * mm, "end": v(-17.09, 14.87) * mm});
            skLineSegment(sketch, "E3.11.3.0", {"start": v(-20.09, 11.87) * mm, "end": v(-17.09, 11.87) * mm});
            skLineSegment(sketch, "E3.11.3.1", {"start": v(-20.09, 8.87) * mm, "end": v(-17.09, 8.87) * mm});
            skLineSegment(sketch, "E3.11.3.2", {"start": v(-20.09, 11.87) * mm, "end": v(-20.09, 8.87) * mm});
            skLineSegment(sketch, "E3.11.3.3", {"start": v(-17.09, 11.87) * mm, "end": v(-17.09, 8.87) * mm});
            skLineSegment(sketch, "E3.11.4.0", {"start": v(-20.09, 5.87) * mm, "end": v(-17.09, 5.87) * mm});
            skLineSegment(sketch, "E3.11.4.1", {"start": v(-20.09, 2.87) * mm, "end": v(-17.09, 2.87) * mm});
            skLineSegment(sketch, "E3.11.4.2", {"start": v(-20.09, 5.87) * mm, "end": v(-20.09, 2.87) * mm});
            skLineSegment(sketch, "E3.11.4.3", {"start": v(-17.09, 5.87) * mm, "end": v(-17.09, 2.87) * mm});
            skLineSegment(sketch, "E3.11.5.0", {"start": v(-20.09, -0.13) * mm, "end": v(-17.09, -0.13) * mm});
            skLineSegment(sketch, "E3.11.5.1", {"start": v(-20.09, -3.13) * mm, "end": v(-17.09, -3.13) * mm});
            skLineSegment(sketch, "E3.11.5.2", {"start": v(-20.09, -0.13) * mm, "end": v(-20.09, -3.13) * mm});
            skLineSegment(sketch, "E3.11.5.3", {"start": v(-17.09, -0.13) * mm, "end": v(-17.09, -3.13) * mm});
            skLineSegment(sketch, "E3.11.6.0", {"start": v(-20.09, -6.13) * mm, "end": v(-17.09, -6.13) * mm});
            skLineSegment(sketch, "E3.11.6.1", {"start": v(-20.09, -9.13) * mm, "end": v(-17.09, -9.13) * mm});
            skLineSegment(sketch, "E3.11.6.2", {"start": v(-20.09, -6.13) * mm, "end": v(-20.09, -9.13) * mm});
            skLineSegment(sketch, "E3.11.6.3", {"start": v(-17.09, -6.13) * mm, "end": v(-17.09, -9.13) * mm});
            skLineSegment(sketch, "E3.11.7.0", {"start": v(-20.09, -12.13) * mm, "end": v(-17.09, -12.13) * mm});
            skLineSegment(sketch, "E3.11.7.1", {"start": v(-20.09, -15.13) * mm, "end": v(-17.09, -15.13) * mm});
            skLineSegment(sketch, "E3.11.7.2", {"start": v(-20.09, -12.13) * mm, "end": v(-20.09, -15.13) * mm});
            skLineSegment(sketch, "E3.11.7.3", {"start": v(-17.09, -12.13) * mm, "end": v(-17.09, -15.13) * mm});
            skLineSegment(sketch, "E3.11.8.0", {"start": v(-20.09, -18.13) * mm, "end": v(-17.09, -18.13) * mm});
            skLineSegment(sketch, "E3.11.8.1", {"start": v(-20.09, -21.13) * mm, "end": v(-17.09, -21.13) * mm});
            skLineSegment(sketch, "E3.11.8.2", {"start": v(-20.09, -18.13) * mm, "end": v(-20.09, -21.13) * mm});
            skLineSegment(sketch, "E3.11.8.3", {"start": v(-17.09, -18.13) * mm, "end": v(-17.09, -21.13) * mm});
            skLineSegment(sketch, "E3.11.9.0", {"start": v(-20.09, -24.13) * mm, "end": v(-17.09, -24.13) * mm});
            skLineSegment(sketch, "E3.11.9.1", {"start": v(-20.09, -27.13) * mm, "end": v(-17.09, -27.13) * mm});
            skLineSegment(sketch, "E3.11.9.2", {"start": v(-20.09, -24.13) * mm, "end": v(-20.09, -27.13) * mm});
            skLineSegment(sketch, "E3.11.9.3", {"start": v(-17.09, -24.13) * mm, "end": v(-17.09, -27.13) * mm});
            skLineSegment(sketch, "E3.12.0.0", {"start": v(-14.09, 29.87) * mm, "end": v(-11.09, 29.87) * mm});
            skLineSegment(sketch, "E3.12.0.1", {"start": v(-14.09, 26.87) * mm, "end": v(-11.09, 26.87) * mm});
            skLineSegment(sketch, "E3.12.0.2", {"start": v(-14.09, 29.87) * mm, "end": v(-14.09, 26.87) * mm});
            skLineSegment(sketch, "E3.12.0.3", {"start": v(-11.09, 29.87) * mm, "end": v(-11.09, 26.87) * mm});
            skLineSegment(sketch, "E3.12.1.0", {"start": v(-14.09, 23.87) * mm, "end": v(-11.09, 23.87) * mm});
            skLineSegment(sketch, "E3.12.1.1", {"start": v(-14.09, 20.87) * mm, "end": v(-11.09, 20.87) * mm});
            skLineSegment(sketch, "E3.12.1.2", {"start": v(-14.09, 23.87) * mm, "end": v(-14.09, 20.87) * mm});
            skLineSegment(sketch, "E3.12.1.3", {"start": v(-11.09, 23.87) * mm, "end": v(-11.09, 20.87) * mm});
            skLineSegment(sketch, "E3.12.2.0", {"start": v(-14.09, 17.87) * mm, "end": v(-11.09, 17.87) * mm});
            skLineSegment(sketch, "E3.12.2.1", {"start": v(-14.09, 14.87) * mm, "end": v(-11.09, 14.87) * mm});
            skLineSegment(sketch, "E3.12.2.2", {"start": v(-14.09, 17.87) * mm, "end": v(-14.09, 14.87) * mm});
            skLineSegment(sketch, "E3.12.2.3", {"start": v(-11.09, 17.87) * mm, "end": v(-11.09, 14.87) * mm});
            skLineSegment(sketch, "E3.12.3.0", {"start": v(-14.09, 11.87) * mm, "end": v(-11.09, 11.87) * mm});
            skLineSegment(sketch, "E3.12.3.1", {"start": v(-14.09, 8.87) * mm, "end": v(-11.09, 8.87) * mm});
            skLineSegment(sketch, "E3.12.3.2", {"start": v(-14.09, 11.87) * mm, "end": v(-14.09, 8.87) * mm});
            skLineSegment(sketch, "E3.12.3.3", {"start": v(-11.09, 11.87) * mm, "end": v(-11.09, 8.87) * mm});
            skLineSegment(sketch, "E3.12.4.0", {"start": v(-14.09, 5.87) * mm, "end": v(-11.09, 5.87) * mm});
            skLineSegment(sketch, "E3.12.4.1", {"start": v(-14.09, 2.87) * mm, "end": v(-11.09, 2.87) * mm});
            skLineSegment(sketch, "E3.12.4.2", {"start": v(-14.09, 5.87) * mm, "end": v(-14.09, 2.87) * mm});
            skLineSegment(sketch, "E3.12.4.3", {"start": v(-11.09, 5.87) * mm, "end": v(-11.09, 2.87) * mm});
            skLineSegment(sketch, "E3.12.5.0", {"start": v(-14.09, -0.13) * mm, "end": v(-11.09, -0.13) * mm});
            skLineSegment(sketch, "E3.12.5.1", {"start": v(-14.09, -3.13) * mm, "end": v(-11.09, -3.13) * mm});
            skLineSegment(sketch, "E3.12.5.2", {"start": v(-14.09, -0.13) * mm, "end": v(-14.09, -3.13) * mm});
            skLineSegment(sketch, "E3.12.5.3", {"start": v(-11.09, -0.13) * mm, "end": v(-11.09, -3.13) * mm});
            skLineSegment(sketch, "E3.12.6.0", {"start": v(-14.09, -6.13) * mm, "end": v(-11.09, -6.13) * mm});
            skLineSegment(sketch, "E3.12.6.1", {"start": v(-14.09, -9.13) * mm, "end": v(-11.09, -9.13) * mm});
            skLineSegment(sketch, "E3.12.6.2", {"start": v(-14.09, -6.13) * mm, "end": v(-14.09, -9.13) * mm});
            skLineSegment(sketch, "E3.12.6.3", {"start": v(-11.09, -6.13) * mm, "end": v(-11.09, -9.13) * mm});
            skLineSegment(sketch, "E3.12.7.0", {"start": v(-14.09, -12.13) * mm, "end": v(-11.09, -12.13) * mm});
            skLineSegment(sketch, "E3.12.7.1", {"start": v(-14.09, -15.13) * mm, "end": v(-11.09, -15.13) * mm});
            skLineSegment(sketch, "E3.12.7.2", {"start": v(-14.09, -12.13) * mm, "end": v(-14.09, -15.13) * mm});
            skLineSegment(sketch, "E3.12.7.3", {"start": v(-11.09, -12.13) * mm, "end": v(-11.09, -15.13) * mm});
            skLineSegment(sketch, "E3.12.8.0", {"start": v(-14.09, -18.13) * mm, "end": v(-11.09, -18.13) * mm});
            skLineSegment(sketch, "E3.12.8.1", {"start": v(-14.09, -21.13) * mm, "end": v(-11.09, -21.13) * mm});
            skLineSegment(sketch, "E3.12.8.2", {"start": v(-14.09, -18.13) * mm, "end": v(-14.09, -21.13) * mm});
            skLineSegment(sketch, "E3.12.8.3", {"start": v(-11.09, -18.13) * mm, "end": v(-11.09, -21.13) * mm});
            skLineSegment(sketch, "E3.12.9.0", {"start": v(-14.09, -24.13) * mm, "end": v(-11.09, -24.13) * mm});
            skLineSegment(sketch, "E3.12.9.1", {"start": v(-14.09, -27.13) * mm, "end": v(-11.09, -27.13) * mm});
            skLineSegment(sketch, "E3.12.9.2", {"start": v(-14.09, -24.13) * mm, "end": v(-14.09, -27.13) * mm});
            skLineSegment(sketch, "E3.12.9.3", {"start": v(-11.09, -24.13) * mm, "end": v(-11.09, -27.13) * mm});
            skLineSegment(sketch, "E3.13.0.0", {"start": v(-8.09, 29.87) * mm, "end": v(-5.09, 29.87) * mm});
            skLineSegment(sketch, "E3.13.0.1", {"start": v(-8.09, 26.87) * mm, "end": v(-5.09, 26.87) * mm});
            skLineSegment(sketch, "E3.13.0.2", {"start": v(-8.09, 29.87) * mm, "end": v(-8.09, 26.87) * mm});
            skLineSegment(sketch, "E3.13.0.3", {"start": v(-5.09, 29.87) * mm, "end": v(-5.09, 26.87) * mm});
            skLineSegment(sketch, "E3.13.1.0", {"start": v(-8.09, 23.87) * mm, "end": v(-5.09, 23.87) * mm});
            skLineSegment(sketch, "E3.13.1.1", {"start": v(-8.09, 20.87) * mm, "end": v(-5.09, 20.87) * mm});
            skLineSegment(sketch, "E3.13.1.2", {"start": v(-8.09, 23.87) * mm, "end": v(-8.09, 20.87) * mm});
            skLineSegment(sketch, "E3.13.1.3", {"start": v(-5.09, 23.87) * mm, "end": v(-5.09, 20.87) * mm});
            skLineSegment(sketch, "E3.13.2.0", {"start": v(-8.09, 17.87) * mm, "end": v(-5.09, 17.87) * mm});
            skLineSegment(sketch, "E3.13.2.1", {"start": v(-8.09, 14.87) * mm, "end": v(-5.09, 14.87) * mm});
            skLineSegment(sketch, "E3.13.2.2", {"start": v(-8.09, 17.87) * mm, "end": v(-8.09, 14.87) * mm});
            skLineSegment(sketch, "E3.13.2.3", {"start": v(-5.09, 17.87) * mm, "end": v(-5.09, 14.87) * mm});
            skLineSegment(sketch, "E3.13.3.0", {"start": v(-8.09, 11.87) * mm, "end": v(-5.09, 11.87) * mm});
            skLineSegment(sketch, "E3.13.3.1", {"start": v(-8.09, 8.87) * mm, "end": v(-5.09, 8.87) * mm});
            skLineSegment(sketch, "E3.13.3.2", {"start": v(-8.09, 11.87) * mm, "end": v(-8.09, 8.87) * mm});
            skLineSegment(sketch, "E3.13.3.3", {"start": v(-5.09, 11.87) * mm, "end": v(-5.09, 8.87) * mm});
            skLineSegment(sketch, "E3.13.4.0", {"start": v(-8.09, 5.87) * mm, "end": v(-5.09, 5.87) * mm});
            skLineSegment(sketch, "E3.13.4.1", {"start": v(-8.09, 2.87) * mm, "end": v(-5.09, 2.87) * mm});
            skLineSegment(sketch, "E3.13.4.2", {"start": v(-8.09, 5.87) * mm, "end": v(-8.09, 2.87) * mm});
            skLineSegment(sketch, "E3.13.4.3", {"start": v(-5.09, 5.87) * mm, "end": v(-5.09, 2.87) * mm});
            skLineSegment(sketch, "E3.13.5.0", {"start": v(-8.09, -0.13) * mm, "end": v(-5.09, -0.13) * mm});
            skLineSegment(sketch, "E3.13.5.1", {"start": v(-8.09, -3.13) * mm, "end": v(-5.09, -3.13) * mm});
            skLineSegment(sketch, "E3.13.5.2", {"start": v(-8.09, -0.13) * mm, "end": v(-8.09, -3.13) * mm});
            skLineSegment(sketch, "E3.13.5.3", {"start": v(-5.09, -0.13) * mm, "end": v(-5.09, -3.13) * mm});
            skLineSegment(sketch, "E3.13.6.0", {"start": v(-8.09, -6.13) * mm, "end": v(-5.09, -6.13) * mm});
            skLineSegment(sketch, "E3.13.6.1", {"start": v(-8.09, -9.13) * mm, "end": v(-5.09, -9.13) * mm});
            skLineSegment(sketch, "E3.13.6.2", {"start": v(-8.09, -6.13) * mm, "end": v(-8.09, -9.13) * mm});
            skLineSegment(sketch, "E3.13.6.3", {"start": v(-5.09, -6.13) * mm, "end": v(-5.09, -9.13) * mm});
            skLineSegment(sketch, "E3.13.7.0", {"start": v(-8.09, -12.13) * mm, "end": v(-5.09, -12.13) * mm});
            skLineSegment(sketch, "E3.13.7.1", {"start": v(-8.09, -15.13) * mm, "end": v(-5.09, -15.13) * mm});
            skLineSegment(sketch, "E3.13.7.2", {"start": v(-8.09, -12.13) * mm, "end": v(-8.09, -15.13) * mm});
            skLineSegment(sketch, "E3.13.7.3", {"start": v(-5.09, -12.13) * mm, "end": v(-5.09, -15.13) * mm});
            skLineSegment(sketch, "E3.13.8.0", {"start": v(-8.09, -18.13) * mm, "end": v(-5.09, -18.13) * mm});
            skLineSegment(sketch, "E3.13.8.1", {"start": v(-8.09, -21.13) * mm, "end": v(-5.09, -21.13) * mm});
            skLineSegment(sketch, "E3.13.8.2", {"start": v(-8.09, -18.13) * mm, "end": v(-8.09, -21.13) * mm});
            skLineSegment(sketch, "E3.13.8.3", {"start": v(-5.09, -18.13) * mm, "end": v(-5.09, -21.13) * mm});
            skLineSegment(sketch, "E3.13.9.0", {"start": v(-8.09, -24.13) * mm, "end": v(-5.09, -24.13) * mm});
            skLineSegment(sketch, "E3.13.9.1", {"start": v(-8.09, -27.13) * mm, "end": v(-5.09, -27.13) * mm});
            skLineSegment(sketch, "E3.13.9.2", {"start": v(-8.09, -24.13) * mm, "end": v(-8.09, -27.13) * mm});
            skLineSegment(sketch, "E3.13.9.3", {"start": v(-5.09, -24.13) * mm, "end": v(-5.09, -27.13) * mm});
            skLineSegment(sketch, "E3.14.0.0", {"start": v(-2.09, 29.87) * mm, "end": v(0.91, 29.87) * mm});
            skLineSegment(sketch, "E3.14.0.1", {"start": v(-2.09, 26.87) * mm, "end": v(0.91, 26.87) * mm});
            skLineSegment(sketch, "E3.14.0.2", {"start": v(-2.09, 29.87) * mm, "end": v(-2.09, 26.87) * mm});
            skLineSegment(sketch, "E3.14.0.3", {"start": v(0.91, 29.87) * mm, "end": v(0.91, 26.87) * mm});
            skLineSegment(sketch, "E3.14.1.0", {"start": v(-2.09, 23.87) * mm, "end": v(0.91, 23.87) * mm});
            skLineSegment(sketch, "E3.14.1.1", {"start": v(-2.09, 20.87) * mm, "end": v(0.91, 20.87) * mm});
            skLineSegment(sketch, "E3.14.1.2", {"start": v(-2.09, 23.87) * mm, "end": v(-2.09, 20.87) * mm});
            skLineSegment(sketch, "E3.14.1.3", {"start": v(0.91, 23.87) * mm, "end": v(0.91, 20.87) * mm});
            skLineSegment(sketch, "E3.14.2.0", {"start": v(-2.09, 17.87) * mm, "end": v(0.91, 17.87) * mm});
            skLineSegment(sketch, "E3.14.2.1", {"start": v(-2.09, 14.87) * mm, "end": v(0.91, 14.87) * mm});
            skLineSegment(sketch, "E3.14.2.2", {"start": v(-2.09, 17.87) * mm, "end": v(-2.09, 14.87) * mm});
            skLineSegment(sketch, "E3.14.2.3", {"start": v(0.91, 17.87) * mm, "end": v(0.91, 14.87) * mm});
            skLineSegment(sketch, "E3.14.3.0", {"start": v(-2.09, 11.87) * mm, "end": v(0.91, 11.87) * mm});
            skLineSegment(sketch, "E3.14.3.1", {"start": v(-2.09, 8.87) * mm, "end": v(0.91, 8.87) * mm});
            skLineSegment(sketch, "E3.14.3.2", {"start": v(-2.09, 11.87) * mm, "end": v(-2.09, 8.87) * mm});
            skLineSegment(sketch, "E3.14.3.3", {"start": v(0.91, 11.87) * mm, "end": v(0.91, 8.87) * mm});
            skLineSegment(sketch, "E3.14.4.0", {"start": v(-2.09, 5.87) * mm, "end": v(0.91, 5.87) * mm});
            skLineSegment(sketch, "E3.14.4.1", {"start": v(-2.09, 2.87) * mm, "end": v(0.91, 2.87) * mm});
            skLineSegment(sketch, "E3.14.4.2", {"start": v(-2.09, 5.87) * mm, "end": v(-2.09, 2.87) * mm});
            skLineSegment(sketch, "E3.14.4.3", {"start": v(0.91, 5.87) * mm, "end": v(0.91, 2.87) * mm});
            skLineSegment(sketch, "E3.14.5.0", {"start": v(-2.09, -0.13) * mm, "end": v(0.91, -0.13) * mm});
            skLineSegment(sketch, "E3.14.5.1", {"start": v(-2.09, -3.13) * mm, "end": v(0.91, -3.13) * mm});
            skLineSegment(sketch, "E3.14.5.2", {"start": v(-2.09, -0.13) * mm, "end": v(-2.09, -3.13) * mm});
            skLineSegment(sketch, "E3.14.5.3", {"start": v(0.91, -0.13) * mm, "end": v(0.91, -3.13) * mm});
            skLineSegment(sketch, "E3.14.6.0", {"start": v(-2.09, -6.13) * mm, "end": v(0.91, -6.13) * mm});
            skLineSegment(sketch, "E3.14.6.1", {"start": v(-2.09, -9.13) * mm, "end": v(0.91, -9.13) * mm});
            skLineSegment(sketch, "E3.14.6.2", {"start": v(-2.09, -6.13) * mm, "end": v(-2.09, -9.13) * mm});
            skLineSegment(sketch, "E3.14.6.3", {"start": v(0.91, -6.13) * mm, "end": v(0.91, -9.13) * mm});
            skLineSegment(sketch, "E3.14.7.0", {"start": v(-2.09, -12.13) * mm, "end": v(0.91, -12.13) * mm});
            skLineSegment(sketch, "E3.14.7.1", {"start": v(-2.09, -15.13) * mm, "end": v(0.91, -15.13) * mm});
            skLineSegment(sketch, "E3.14.7.2", {"start": v(-2.09, -12.13) * mm, "end": v(-2.09, -15.13) * mm});
            skLineSegment(sketch, "E3.14.7.3", {"start": v(0.91, -12.13) * mm, "end": v(0.91, -15.13) * mm});
            skLineSegment(sketch, "E3.14.8.0", {"start": v(-2.09, -18.13) * mm, "end": v(0.91, -18.13) * mm});
            skLineSegment(sketch, "E3.14.8.1", {"start": v(-2.09, -21.13) * mm, "end": v(0.91, -21.13) * mm});
            skLineSegment(sketch, "E3.14.8.2", {"start": v(-2.09, -18.13) * mm, "end": v(-2.09, -21.13) * mm});
            skLineSegment(sketch, "E3.14.8.3", {"start": v(0.91, -18.13) * mm, "end": v(0.91, -21.13) * mm});
            skLineSegment(sketch, "E3.14.9.0", {"start": v(-2.09, -24.13) * mm, "end": v(0.91, -24.13) * mm});
            skLineSegment(sketch, "E3.14.9.1", {"start": v(-2.09, -27.13) * mm, "end": v(0.91, -27.13) * mm});
            skLineSegment(sketch, "E3.14.9.2", {"start": v(-2.09, -24.13) * mm, "end": v(-2.09, -27.13) * mm});
            skLineSegment(sketch, "E3.14.9.3", {"start": v(0.91, -24.13) * mm, "end": v(0.91, -27.13) * mm});
            skLineSegment(sketch, "E3.15.0.0", {"start": v(3.91, 29.87) * mm, "end": v(6.91, 29.87) * mm});
            skLineSegment(sketch, "E3.15.0.1", {"start": v(3.91, 26.87) * mm, "end": v(6.91, 26.87) * mm});
            skLineSegment(sketch, "E3.15.0.2", {"start": v(3.91, 29.87) * mm, "end": v(3.91, 26.87) * mm});
            skLineSegment(sketch, "E3.15.0.3", {"start": v(6.91, 29.87) * mm, "end": v(6.91, 26.87) * mm});
            skLineSegment(sketch, "E3.15.1.0", {"start": v(3.91, 23.87) * mm, "end": v(6.91, 23.87) * mm});
            skLineSegment(sketch, "E3.15.1.1", {"start": v(3.91, 20.87) * mm, "end": v(6.91, 20.87) * mm});
            skLineSegment(sketch, "E3.15.1.2", {"start": v(3.91, 23.87) * mm, "end": v(3.91, 20.87) * mm});
            skLineSegment(sketch, "E3.15.1.3", {"start": v(6.91, 23.87) * mm, "end": v(6.91, 20.87) * mm});
            skLineSegment(sketch, "E3.15.2.0", {"start": v(3.91, 17.87) * mm, "end": v(6.91, 17.87) * mm});
            skLineSegment(sketch, "E3.15.2.1", {"start": v(3.91, 14.87) * mm, "end": v(6.91, 14.87) * mm});
            skLineSegment(sketch, "E3.15.2.2", {"start": v(3.91, 17.87) * mm, "end": v(3.91, 14.87) * mm});
            skLineSegment(sketch, "E3.15.2.3", {"start": v(6.91, 17.87) * mm, "end": v(6.91, 14.87) * mm});
            skLineSegment(sketch, "E3.15.3.0", {"start": v(3.91, 11.87) * mm, "end": v(6.91, 11.87) * mm});
            skLineSegment(sketch, "E3.15.3.1", {"start": v(3.91, 8.87) * mm, "end": v(6.91, 8.87) * mm});
            skLineSegment(sketch, "E3.15.3.2", {"start": v(3.91, 11.87) * mm, "end": v(3.91, 8.87) * mm});
            skLineSegment(sketch, "E3.15.3.3", {"start": v(6.91, 11.87) * mm, "end": v(6.91, 8.87) * mm});
            skLineSegment(sketch, "E3.15.4.0", {"start": v(3.91, 5.87) * mm, "end": v(6.91, 5.87) * mm});
            skLineSegment(sketch, "E3.15.4.1", {"start": v(3.91, 2.87) * mm, "end": v(6.91, 2.87) * mm});
            skLineSegment(sketch, "E3.15.4.2", {"start": v(3.91, 5.87) * mm, "end": v(3.91, 2.87) * mm});
            skLineSegment(sketch, "E3.15.4.3", {"start": v(6.91, 5.87) * mm, "end": v(6.91, 2.87) * mm});
            skLineSegment(sketch, "E3.15.5.0", {"start": v(3.91, -0.13) * mm, "end": v(6.91, -0.13) * mm});
            skLineSegment(sketch, "E3.15.5.1", {"start": v(3.91, -3.13) * mm, "end": v(6.91, -3.13) * mm});
            skLineSegment(sketch, "E3.15.5.2", {"start": v(3.91, -0.13) * mm, "end": v(3.91, -3.13) * mm});
            skLineSegment(sketch, "E3.15.5.3", {"start": v(6.91, -0.13) * mm, "end": v(6.91, -3.13) * mm});
            skLineSegment(sketch, "E3.15.6.0", {"start": v(3.91, -6.13) * mm, "end": v(6.91, -6.13) * mm});
            skLineSegment(sketch, "E3.15.6.1", {"start": v(3.91, -9.13) * mm, "end": v(6.91, -9.13) * mm});
            skLineSegment(sketch, "E3.15.6.2", {"start": v(3.91, -6.13) * mm, "end": v(3.91, -9.13) * mm});
            skLineSegment(sketch, "E3.15.6.3", {"start": v(6.91, -6.13) * mm, "end": v(6.91, -9.13) * mm});
            skLineSegment(sketch, "E3.15.7.0", {"start": v(3.91, -12.13) * mm, "end": v(6.91, -12.13) * mm});
            skLineSegment(sketch, "E3.15.7.1", {"start": v(3.91, -15.13) * mm, "end": v(6.91, -15.13) * mm});
            skLineSegment(sketch, "E3.15.7.2", {"start": v(3.91, -12.13) * mm, "end": v(3.91, -15.13) * mm});
            skLineSegment(sketch, "E3.15.7.3", {"start": v(6.91, -12.13) * mm, "end": v(6.91, -15.13) * mm});
            skLineSegment(sketch, "E3.15.8.0", {"start": v(3.91, -18.13) * mm, "end": v(6.91, -18.13) * mm});
            skLineSegment(sketch, "E3.15.8.1", {"start": v(3.91, -21.13) * mm, "end": v(6.91, -21.13) * mm});
            skLineSegment(sketch, "E3.15.8.2", {"start": v(3.91, -18.13) * mm, "end": v(3.91, -21.13) * mm});
            skLineSegment(sketch, "E3.15.8.3", {"start": v(6.91, -18.13) * mm, "end": v(6.91, -21.13) * mm});
            skLineSegment(sketch, "E3.15.9.0", {"start": v(3.91, -24.13) * mm, "end": v(6.91, -24.13) * mm});
            skLineSegment(sketch, "E3.15.9.1", {"start": v(3.91, -27.13) * mm, "end": v(6.91, -27.13) * mm});
            skLineSegment(sketch, "E3.15.9.2", {"start": v(3.91, -24.13) * mm, "end": v(3.91, -27.13) * mm});
            skLineSegment(sketch, "E3.15.9.3", {"start": v(6.91, -24.13) * mm, "end": v(6.91, -27.13) * mm});
            skLineSegment(sketch, "E3.direction1", {"start": v(-86.09, 26.87) * mm, "end": v(-80.09, 26.87) * mm, "construction": true});
            skLineSegment(sketch, "E3.direction2", {"start": v(-86.09, 26.87) * mm, "end": v(-86.09, 20.87) * mm, "construction": true});
            skLineSegment(sketch, "E4.0.0.10", {"start": v(-86.09, -30.13) * mm, "end": v(-83.09, -30.13) * mm});
            skLineSegment(sketch, "E4.3.0.10", {"start": v(-86.09, -33.13) * mm, "end": v(-83.09, -33.13) * mm});
            skLineSegment(sketch, "E4.6.0.10", {"start": v(-86.09, -30.13) * mm, "end": v(-86.09, -33.13) * mm});
            skLineSegment(sketch, "E4.9.0.10", {"start": v(-83.09, -30.13) * mm, "end": v(-83.09, -33.13) * mm});
            skLineSegment(sketch, "E4.0.1.10", {"start": v(-80.09, -30.13) * mm, "end": v(-77.09, -30.13) * mm});
            skLineSegment(sketch, "E4.3.1.10", {"start": v(-80.09, -33.13) * mm, "end": v(-77.09, -33.13) * mm});
            skLineSegment(sketch, "E4.6.1.10", {"start": v(-80.09, -30.13) * mm, "end": v(-80.09, -33.13) * mm});
            skLineSegment(sketch, "E4.9.1.10", {"start": v(-77.09, -30.13) * mm, "end": v(-77.09, -33.13) * mm});
            skLineSegment(sketch, "E4.0.2.10", {"start": v(-74.09, -30.13) * mm, "end": v(-71.09, -30.13) * mm});
            skLineSegment(sketch, "E4.3.2.10", {"start": v(-74.09, -33.13) * mm, "end": v(-71.09, -33.13) * mm});
            skLineSegment(sketch, "E4.6.2.10", {"start": v(-74.09, -30.13) * mm, "end": v(-74.09, -33.13) * mm});
            skLineSegment(sketch, "E4.9.2.10", {"start": v(-71.09, -30.13) * mm, "end": v(-71.09, -33.13) * mm});
            skLineSegment(sketch, "E4.0.3.10", {"start": v(-68.09, -30.13) * mm, "end": v(-65.09, -30.13) * mm});
            skLineSegment(sketch, "E4.3.3.10", {"start": v(-68.09, -33.13) * mm, "end": v(-65.09, -33.13) * mm});
            skLineSegment(sketch, "E4.6.3.10", {"start": v(-68.09, -30.13) * mm, "end": v(-68.09, -33.13) * mm});
            skLineSegment(sketch, "E4.9.3.10", {"start": v(-65.09, -30.13) * mm, "end": v(-65.09, -33.13) * mm});
            skLineSegment(sketch, "E4.0.4.10", {"start": v(-62.09, -30.13) * mm, "end": v(-59.09, -30.13) * mm});
            skLineSegment(sketch, "E4.3.4.10", {"start": v(-62.09, -33.13) * mm, "end": v(-59.09, -33.13) * mm});
            skLineSegment(sketch, "E4.6.4.10", {"start": v(-62.09, -30.13) * mm, "end": v(-62.09, -33.13) * mm});
            skLineSegment(sketch, "E4.9.4.10", {"start": v(-59.09, -30.13) * mm, "end": v(-59.09, -33.13) * mm});
            skLineSegment(sketch, "E4.0.5.10", {"start": v(-56.09, -30.13) * mm, "end": v(-53.09, -30.13) * mm});
            skLineSegment(sketch, "E4.3.5.10", {"start": v(-56.09, -33.13) * mm, "end": v(-53.09, -33.13) * mm});
            skLineSegment(sketch, "E4.6.5.10", {"start": v(-56.09, -30.13) * mm, "end": v(-56.09, -33.13) * mm});
            skLineSegment(sketch, "E4.9.5.10", {"start": v(-53.09, -30.13) * mm, "end": v(-53.09, -33.13) * mm});
            skLineSegment(sketch, "E4.0.6.10", {"start": v(-50.09, -30.13) * mm, "end": v(-47.09, -30.13) * mm});
            skLineSegment(sketch, "E4.3.6.10", {"start": v(-50.09, -33.13) * mm, "end": v(-47.09, -33.13) * mm});
            skLineSegment(sketch, "E4.6.6.10", {"start": v(-50.09, -30.13) * mm, "end": v(-50.09, -33.13) * mm});
            skLineSegment(sketch, "E4.9.6.10", {"start": v(-47.09, -30.13) * mm, "end": v(-47.09, -33.13) * mm});
            skLineSegment(sketch, "E4.0.7.10", {"start": v(-44.09, -30.13) * mm, "end": v(-41.09, -30.13) * mm});
            skLineSegment(sketch, "E4.3.7.10", {"start": v(-44.09, -33.13) * mm, "end": v(-41.09, -33.13) * mm});
            skLineSegment(sketch, "E4.6.7.10", {"start": v(-44.09, -30.13) * mm, "end": v(-44.09, -33.13) * mm});
            skLineSegment(sketch, "E4.9.7.10", {"start": v(-41.09, -30.13) * mm, "end": v(-41.09, -33.13) * mm});
            skLineSegment(sketch, "E4.0.8.10", {"start": v(-38.09, -30.13) * mm, "end": v(-35.09, -30.13) * mm});
            skLineSegment(sketch, "E4.3.8.10", {"start": v(-38.09, -33.13) * mm, "end": v(-35.09, -33.13) * mm});
            skLineSegment(sketch, "E4.6.8.10", {"start": v(-38.09, -30.13) * mm, "end": v(-38.09, -33.13) * mm});
            skLineSegment(sketch, "E4.9.8.10", {"start": v(-35.09, -30.13) * mm, "end": v(-35.09, -33.13) * mm});
            skLineSegment(sketch, "E4.0.9.10", {"start": v(-32.09, -30.13) * mm, "end": v(-29.09, -30.13) * mm});
            skLineSegment(sketch, "E4.3.9.10", {"start": v(-32.09, -33.13) * mm, "end": v(-29.09, -33.13) * mm});
            skLineSegment(sketch, "E4.6.9.10", {"start": v(-32.09, -30.13) * mm, "end": v(-32.09, -33.13) * mm});
            skLineSegment(sketch, "E4.9.9.10", {"start": v(-29.09, -30.13) * mm, "end": v(-29.09, -33.13) * mm});
            skLineSegment(sketch, "E4.0.10.10", {"start": v(-26.09, -30.13) * mm, "end": v(-23.09, -30.13) * mm});
            skLineSegment(sketch, "E4.3.10.10", {"start": v(-26.09, -33.13) * mm, "end": v(-23.09, -33.13) * mm});
            skLineSegment(sketch, "E4.6.10.10", {"start": v(-26.09, -30.13) * mm, "end": v(-26.09, -33.13) * mm});
            skLineSegment(sketch, "E4.9.10.10", {"start": v(-23.09, -30.13) * mm, "end": v(-23.09, -33.13) * mm});
            skLineSegment(sketch, "E4.0.11.10", {"start": v(-20.09, -30.13) * mm, "end": v(-17.09, -30.13) * mm});
            skLineSegment(sketch, "E4.3.11.10", {"start": v(-20.09, -33.13) * mm, "end": v(-17.09, -33.13) * mm});
            skLineSegment(sketch, "E4.6.11.10", {"start": v(-20.09, -30.13) * mm, "end": v(-20.09, -33.13) * mm});
            skLineSegment(sketch, "E4.9.11.10", {"start": v(-17.09, -30.13) * mm, "end": v(-17.09, -33.13) * mm});
            skLineSegment(sketch, "E4.0.12.10", {"start": v(-14.09, -30.13) * mm, "end": v(-11.09, -30.13) * mm});
            skLineSegment(sketch, "E4.3.12.10", {"start": v(-14.09, -33.13) * mm, "end": v(-11.09, -33.13) * mm});
            skLineSegment(sketch, "E4.6.12.10", {"start": v(-14.09, -30.13) * mm, "end": v(-14.09, -33.13) * mm});
            skLineSegment(sketch, "E4.9.12.10", {"start": v(-11.09, -30.13) * mm, "end": v(-11.09, -33.13) * mm});
            skLineSegment(sketch, "E4.0.13.10", {"start": v(-8.09, -30.13) * mm, "end": v(-5.09, -30.13) * mm});
            skLineSegment(sketch, "E4.3.13.10", {"start": v(-8.09, -33.13) * mm, "end": v(-5.09, -33.13) * mm});
            skLineSegment(sketch, "E4.6.13.10", {"start": v(-8.09, -30.13) * mm, "end": v(-8.09, -33.13) * mm});
            skLineSegment(sketch, "E4.9.13.10", {"start": v(-5.09, -30.13) * mm, "end": v(-5.09, -33.13) * mm});
            skLineSegment(sketch, "E4.0.14.10", {"start": v(-2.09, -30.13) * mm, "end": v(0.91, -30.13) * mm});
            skLineSegment(sketch, "E4.3.14.10", {"start": v(-2.09, -33.13) * mm, "end": v(0.91, -33.13) * mm});
            skLineSegment(sketch, "E4.6.14.10", {"start": v(-2.09, -30.13) * mm, "end": v(-2.09, -33.13) * mm});
            skLineSegment(sketch, "E4.9.14.10", {"start": v(0.91, -30.13) * mm, "end": v(0.91, -33.13) * mm});
            skLineSegment(sketch, "E4.0.15.10", {"start": v(3.91, -30.13) * mm, "end": v(6.91, -30.13) * mm});
            skLineSegment(sketch, "E4.3.15.10", {"start": v(3.91, -33.13) * mm, "end": v(6.91, -33.13) * mm});
            skLineSegment(sketch, "E4.6.15.10", {"start": v(3.91, -30.13) * mm, "end": v(3.91, -33.13) * mm});
            skLineSegment(sketch, "E4.9.15.10", {"start": v(6.91, -30.13) * mm, "end": v(6.91, -33.13) * mm});
            skSolve(sketch);
        }
        {
            var Q0;
            {var subQ1=sQuery(id+"F0.wireOp",EDGE,"E0.bottom");Q0=makeQuery(id+"F0.imprint","IMPRINT",FACE,{"disambiguationData":[TD([[makeQuery(id+"F0.imprint","IMPRINT",EDGE,{"derivedFrom":subQ1}),-1.0]])]});}
            extrude(context, id + "F1", {"entities" : qUnion([Q0]), "depth" : 0.6 * mm});
        }
        {
            var Q0;
            {var subQ2=sQuery(id+"F0.wireOp",EDGE,"E0.bottom");Q0=makeQuery(id+"F0.imprint","IMPRINT",FACE,{"disambiguationData":[TD([[makeQuery(id+"F0.imprint","IMPRINT",EDGE,{"derivedFrom":subQ2}),1.0]])]});}
            var Q1;
            Q1=sQuery(id+"F0.wireOp",EDGE,"E0.top");
            var Q2;
            Q2=sQuery(id+"F0.wireOp",EDGE,"E1.bottom");
            extrude(context, id + "F2", {"entities" : qUnion([Q0]), "operationType" : NewBodyOperationType.ADD, "surfaceEntities" : qUnion([Q1, Q2]), "depth" : 10 * mm});
        }
    });
